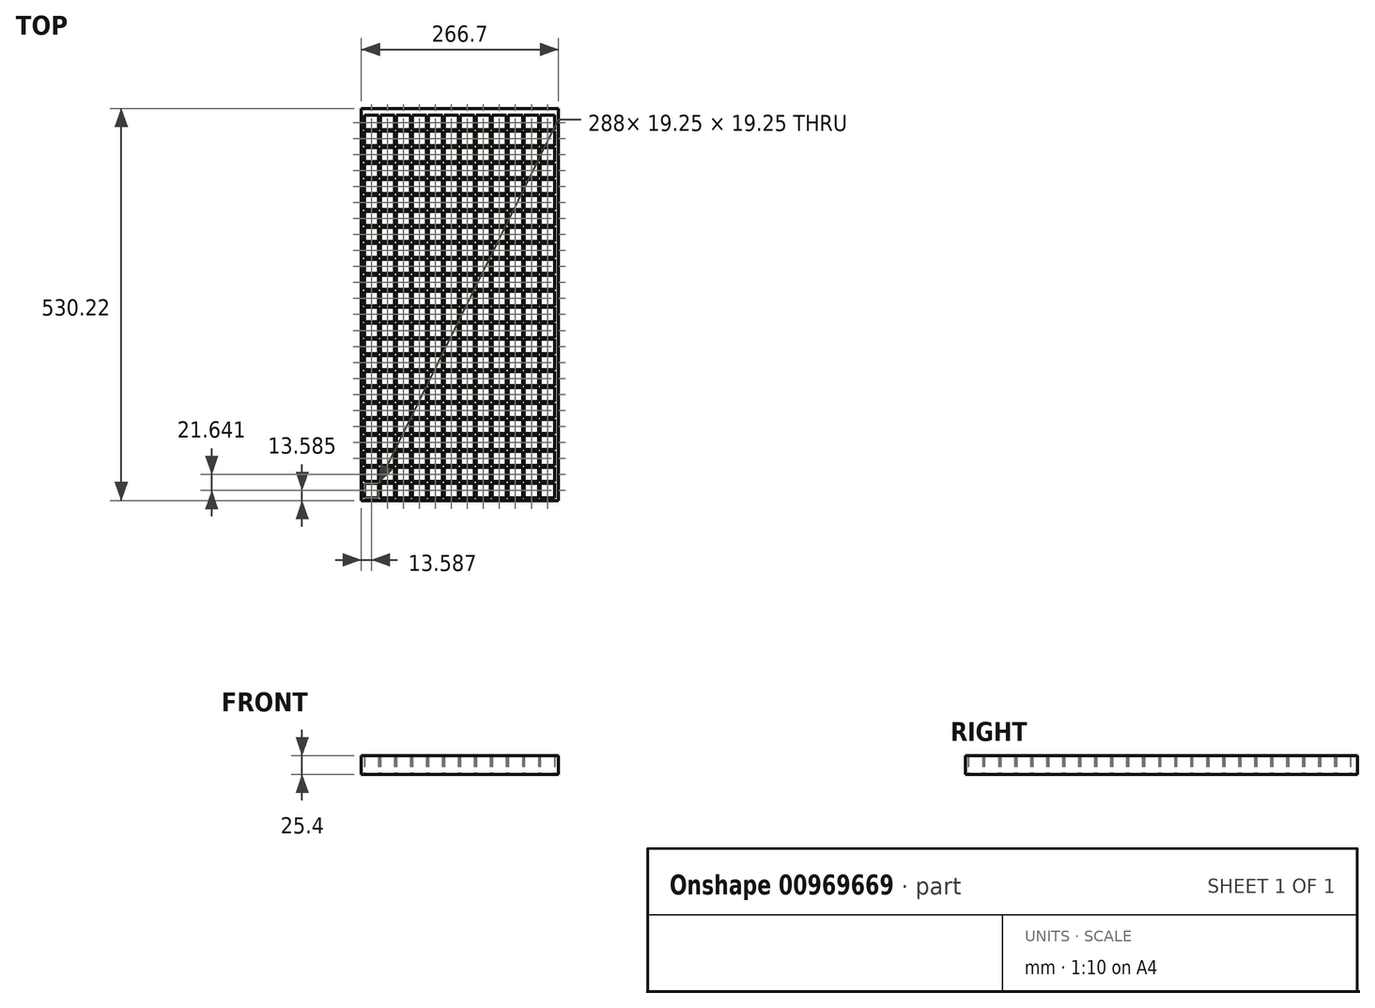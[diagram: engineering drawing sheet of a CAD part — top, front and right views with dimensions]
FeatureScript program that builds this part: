
annotation { "Feature Type Name" : "Feature", "Feature Type Description" : "" }
export const myFeature = defineFeature(function(context is Context, id is Id, definition is map)
    precondition{}
    {
        {
            var Q0;
            Q0=qCreatedBy(makeId("Top.planeOp"),FACE);
            var sketch = newSketch(context, id + "F0", { "sketchPlane" : qUnion([Q0])});
            skLineSegment(sketch, "E0.bottom", {"start": v(-120.4, -242.61) * mm, "end": v(146.3, -242.61) * mm});
            skLineSegment(sketch, "E0.top", {"start": v(-120.4, 287.61) * mm, "end": v(146.3, 287.61) * mm});
            skLineSegment(sketch, "E0.left", {"start": v(-120.4, -242.61) * mm, "end": v(-120.4, 287.61) * mm});
            skLineSegment(sketch, "E0.right", {"start": v(146.3, -242.61) * mm, "end": v(146.3, 287.61) * mm});
            skLineSegment(sketch, "E1.bottom", {"start": v(-116.43, -219.4) * mm, "end": v(-97.18, -219.4) * mm});
            skLineSegment(sketch, "E1.top", {"start": v(-116.43, -238.65) * mm, "end": v(-97.18, -238.65) * mm});
            skLineSegment(sketch, "E1.left", {"start": v(-116.43, -219.4) * mm, "end": v(-116.43, -238.65) * mm});
            skLineSegment(sketch, "E1.right", {"start": v(-97.18, -219.4) * mm, "end": v(-97.18, -238.65) * mm});
            skLineSegment(sketch, "E2.0.1.0", {"start": v(-116.43, -197.76) * mm, "end": v(-97.18, -197.76) * mm});
            skLineSegment(sketch, "E2.0.1.1", {"start": v(-116.43, -217.01) * mm, "end": v(-97.18, -217.01) * mm});
            skLineSegment(sketch, "E2.0.1.2", {"start": v(-116.43, -197.76) * mm, "end": v(-116.43, -217.01) * mm});
            skLineSegment(sketch, "E2.0.1.3", {"start": v(-97.18, -197.76) * mm, "end": v(-97.18, -217.01) * mm});
            skLineSegment(sketch, "E2.0.2.0", {"start": v(-116.43, -176.12) * mm, "end": v(-97.18, -176.12) * mm});
            skLineSegment(sketch, "E2.0.2.1", {"start": v(-116.43, -195.37) * mm, "end": v(-97.18, -195.37) * mm});
            skLineSegment(sketch, "E2.0.2.2", {"start": v(-116.43, -176.12) * mm, "end": v(-116.43, -195.37) * mm});
            skLineSegment(sketch, "E2.0.2.3", {"start": v(-97.18, -176.12) * mm, "end": v(-97.18, -195.37) * mm});
            skLineSegment(sketch, "E2.0.3.0", {"start": v(-116.43, -154.48) * mm, "end": v(-97.18, -154.48) * mm});
            skLineSegment(sketch, "E2.0.3.1", {"start": v(-116.43, -173.73) * mm, "end": v(-97.18, -173.73) * mm});
            skLineSegment(sketch, "E2.0.3.2", {"start": v(-116.43, -154.48) * mm, "end": v(-116.43, -173.73) * mm});
            skLineSegment(sketch, "E2.0.3.3", {"start": v(-97.18, -154.48) * mm, "end": v(-97.18, -173.73) * mm});
            skLineSegment(sketch, "E2.0.4.0", {"start": v(-116.43, -132.84) * mm, "end": v(-97.18, -132.84) * mm});
            skLineSegment(sketch, "E2.0.4.1", {"start": v(-116.43, -152.09) * mm, "end": v(-97.18, -152.09) * mm});
            skLineSegment(sketch, "E2.0.4.2", {"start": v(-116.43, -132.84) * mm, "end": v(-116.43, -152.09) * mm});
            skLineSegment(sketch, "E2.0.4.3", {"start": v(-97.18, -132.84) * mm, "end": v(-97.18, -152.09) * mm});
            skLineSegment(sketch, "E2.0.5.0", {"start": v(-116.43, -111.2) * mm, "end": v(-97.18, -111.2) * mm});
            skLineSegment(sketch, "E2.0.5.1", {"start": v(-116.43, -130.45) * mm, "end": v(-97.18, -130.45) * mm});
            skLineSegment(sketch, "E2.0.5.2", {"start": v(-116.43, -111.2) * mm, "end": v(-116.43, -130.45) * mm});
            skLineSegment(sketch, "E2.0.5.3", {"start": v(-97.18, -111.2) * mm, "end": v(-97.18, -130.45) * mm});
            skLineSegment(sketch, "E2.0.6.0", {"start": v(-116.43, -89.55) * mm, "end": v(-97.18, -89.55) * mm});
            skLineSegment(sketch, "E2.0.6.1", {"start": v(-116.43, -108.8) * mm, "end": v(-97.18, -108.8) * mm});
            skLineSegment(sketch, "E2.0.6.2", {"start": v(-116.43, -89.55) * mm, "end": v(-116.43, -108.8) * mm});
            skLineSegment(sketch, "E2.0.6.3", {"start": v(-97.18, -89.55) * mm, "end": v(-97.18, -108.8) * mm});
            skLineSegment(sketch, "E2.0.7.0", {"start": v(-116.43, -67.91) * mm, "end": v(-97.18, -67.91) * mm});
            skLineSegment(sketch, "E2.0.7.1", {"start": v(-116.43, -87.17) * mm, "end": v(-97.18, -87.17) * mm});
            skLineSegment(sketch, "E2.0.7.2", {"start": v(-116.43, -67.91) * mm, "end": v(-116.43, -87.17) * mm});
            skLineSegment(sketch, "E2.0.7.3", {"start": v(-97.18, -67.91) * mm, "end": v(-97.18, -87.17) * mm});
            skLineSegment(sketch, "E2.0.8.0", {"start": v(-116.43, -46.27) * mm, "end": v(-97.18, -46.27) * mm});
            skLineSegment(sketch, "E2.0.8.1", {"start": v(-116.43, -65.53) * mm, "end": v(-97.18, -65.53) * mm});
            skLineSegment(sketch, "E2.0.8.2", {"start": v(-116.43, -46.27) * mm, "end": v(-116.43, -65.53) * mm});
            skLineSegment(sketch, "E2.0.8.3", {"start": v(-97.18, -46.27) * mm, "end": v(-97.18, -65.53) * mm});
            skLineSegment(sketch, "E2.0.9.0", {"start": v(-116.43, -24.63) * mm, "end": v(-97.18, -24.63) * mm});
            skLineSegment(sketch, "E2.0.9.1", {"start": v(-116.43, -43.88) * mm, "end": v(-97.18, -43.88) * mm});
            skLineSegment(sketch, "E2.0.9.2", {"start": v(-116.43, -24.63) * mm, "end": v(-116.43, -43.88) * mm});
            skLineSegment(sketch, "E2.0.9.3", {"start": v(-97.18, -24.63) * mm, "end": v(-97.18, -43.88) * mm});
            skLineSegment(sketch, "E2.0.10.0", {"start": v(-116.43, -3) * mm, "end": v(-97.18, -3) * mm});
            skLineSegment(sketch, "E2.0.10.1", {"start": v(-116.43, -22.24) * mm, "end": v(-97.18, -22.24) * mm});
            skLineSegment(sketch, "E2.0.10.2", {"start": v(-116.43, -3) * mm, "end": v(-116.43, -22.24) * mm});
            skLineSegment(sketch, "E2.0.10.3", {"start": v(-97.18, -3) * mm, "end": v(-97.18, -22.24) * mm});
            skLineSegment(sketch, "E2.0.11.0", {"start": v(-116.43, 18.65) * mm, "end": v(-97.18, 18.65) * mm});
            skLineSegment(sketch, "E2.0.11.1", {"start": v(-116.43, -0.6) * mm, "end": v(-97.18, -0.6) * mm});
            skLineSegment(sketch, "E2.0.11.2", {"start": v(-116.43, 18.65) * mm, "end": v(-116.43, -0.6) * mm});
            skLineSegment(sketch, "E2.0.11.3", {"start": v(-97.18, 18.65) * mm, "end": v(-97.18, -0.6) * mm});
            skLineSegment(sketch, "E2.0.12.0", {"start": v(-116.43, 40.3) * mm, "end": v(-97.18, 40.3) * mm});
            skLineSegment(sketch, "E2.0.12.1", {"start": v(-116.43, 21.04) * mm, "end": v(-97.18, 21.04) * mm});
            skLineSegment(sketch, "E2.0.12.2", {"start": v(-116.43, 40.3) * mm, "end": v(-116.43, 21.04) * mm});
            skLineSegment(sketch, "E2.0.12.3", {"start": v(-97.18, 40.3) * mm, "end": v(-97.18, 21.04) * mm});
            skLineSegment(sketch, "E2.0.13.0", {"start": v(-116.43, 61.93) * mm, "end": v(-97.18, 61.93) * mm});
            skLineSegment(sketch, "E2.0.13.1", {"start": v(-116.43, 42.68) * mm, "end": v(-97.18, 42.68) * mm});
            skLineSegment(sketch, "E2.0.13.2", {"start": v(-116.43, 61.93) * mm, "end": v(-116.43, 42.68) * mm});
            skLineSegment(sketch, "E2.0.13.3", {"start": v(-97.18, 61.93) * mm, "end": v(-97.18, 42.68) * mm});
            skLineSegment(sketch, "E2.0.14.0", {"start": v(-116.43, 83.57) * mm, "end": v(-97.18, 83.57) * mm});
            skLineSegment(sketch, "E2.0.14.1", {"start": v(-116.43, 64.32) * mm, "end": v(-97.18, 64.32) * mm});
            skLineSegment(sketch, "E2.0.14.2", {"start": v(-116.43, 83.57) * mm, "end": v(-116.43, 64.32) * mm});
            skLineSegment(sketch, "E2.0.14.3", {"start": v(-97.18, 83.57) * mm, "end": v(-97.18, 64.32) * mm});
            skLineSegment(sketch, "E2.0.15.0", {"start": v(-116.43, 105.21) * mm, "end": v(-97.18, 105.21) * mm});
            skLineSegment(sketch, "E2.0.15.1", {"start": v(-116.43, 85.96) * mm, "end": v(-97.18, 85.96) * mm});
            skLineSegment(sketch, "E2.0.15.2", {"start": v(-116.43, 105.21) * mm, "end": v(-116.43, 85.96) * mm});
            skLineSegment(sketch, "E2.0.15.3", {"start": v(-97.18, 105.21) * mm, "end": v(-97.18, 85.96) * mm});
            skLineSegment(sketch, "E2.0.16.0", {"start": v(-116.43, 126.85) * mm, "end": v(-97.18, 126.85) * mm});
            skLineSegment(sketch, "E2.0.16.1", {"start": v(-116.43, 107.6) * mm, "end": v(-97.18, 107.6) * mm});
            skLineSegment(sketch, "E2.0.16.2", {"start": v(-116.43, 126.85) * mm, "end": v(-116.43, 107.6) * mm});
            skLineSegment(sketch, "E2.0.16.3", {"start": v(-97.18, 126.85) * mm, "end": v(-97.18, 107.6) * mm});
            skLineSegment(sketch, "E2.0.17.0", {"start": v(-116.43, 148.5) * mm, "end": v(-97.18, 148.5) * mm});
            skLineSegment(sketch, "E2.0.17.1", {"start": v(-116.43, 129.24) * mm, "end": v(-97.18, 129.24) * mm});
            skLineSegment(sketch, "E2.0.17.2", {"start": v(-116.43, 148.5) * mm, "end": v(-116.43, 129.24) * mm});
            skLineSegment(sketch, "E2.0.17.3", {"start": v(-97.18, 148.5) * mm, "end": v(-97.18, 129.24) * mm});
            skLineSegment(sketch, "E2.0.18.0", {"start": v(-116.43, 170.14) * mm, "end": v(-97.18, 170.14) * mm});
            skLineSegment(sketch, "E2.0.18.1", {"start": v(-116.43, 150.88) * mm, "end": v(-97.18, 150.88) * mm});
            skLineSegment(sketch, "E2.0.18.2", {"start": v(-116.43, 170.14) * mm, "end": v(-116.43, 150.88) * mm});
            skLineSegment(sketch, "E2.0.18.3", {"start": v(-97.18, 170.14) * mm, "end": v(-97.18, 150.88) * mm});
            skLineSegment(sketch, "E2.0.19.0", {"start": v(-116.43, 191.78) * mm, "end": v(-97.18, 191.78) * mm});
            skLineSegment(sketch, "E2.0.19.1", {"start": v(-116.43, 172.52) * mm, "end": v(-97.18, 172.52) * mm});
            skLineSegment(sketch, "E2.0.19.2", {"start": v(-116.43, 191.78) * mm, "end": v(-116.43, 172.52) * mm});
            skLineSegment(sketch, "E2.0.19.3", {"start": v(-97.18, 191.78) * mm, "end": v(-97.18, 172.52) * mm});
            skLineSegment(sketch, "E2.0.20.0", {"start": v(-116.43, 213.42) * mm, "end": v(-97.18, 213.42) * mm});
            skLineSegment(sketch, "E2.0.20.1", {"start": v(-116.43, 194.16) * mm, "end": v(-97.18, 194.16) * mm});
            skLineSegment(sketch, "E2.0.20.2", {"start": v(-116.43, 213.42) * mm, "end": v(-116.43, 194.16) * mm});
            skLineSegment(sketch, "E2.0.20.3", {"start": v(-97.18, 213.42) * mm, "end": v(-97.18, 194.16) * mm});
            skLineSegment(sketch, "E2.0.21.0", {"start": v(-116.43, 235.06) * mm, "end": v(-97.18, 235.06) * mm});
            skLineSegment(sketch, "E2.0.21.1", {"start": v(-116.43, 215.8) * mm, "end": v(-97.18, 215.8) * mm});
            skLineSegment(sketch, "E2.0.21.2", {"start": v(-116.43, 235.06) * mm, "end": v(-116.43, 215.8) * mm});
            skLineSegment(sketch, "E2.0.21.3", {"start": v(-97.18, 235.06) * mm, "end": v(-97.18, 215.8) * mm});
            skLineSegment(sketch, "E2.0.22.0", {"start": v(-116.43, 256.7) * mm, "end": v(-97.18, 256.7) * mm});
            skLineSegment(sketch, "E2.0.22.1", {"start": v(-116.43, 237.45) * mm, "end": v(-97.18, 237.45) * mm});
            skLineSegment(sketch, "E2.0.22.2", {"start": v(-116.43, 256.7) * mm, "end": v(-116.43, 237.45) * mm});
            skLineSegment(sketch, "E2.0.22.3", {"start": v(-97.18, 256.7) * mm, "end": v(-97.18, 237.45) * mm});
            skLineSegment(sketch, "E2.0.23.0", {"start": v(-116.43, 278.34) * mm, "end": v(-97.18, 278.34) * mm});
            skLineSegment(sketch, "E2.0.23.1", {"start": v(-116.43, 259.09) * mm, "end": v(-97.18, 259.09) * mm});
            skLineSegment(sketch, "E2.0.23.2", {"start": v(-116.43, 278.34) * mm, "end": v(-116.43, 259.09) * mm});
            skLineSegment(sketch, "E2.0.23.3", {"start": v(-97.18, 278.34) * mm, "end": v(-97.18, 259.09) * mm});
            skLineSegment(sketch, "E2.1.0.0", {"start": v(-94.79, -219.4) * mm, "end": v(-75.54, -219.4) * mm});
            skLineSegment(sketch, "E2.1.0.1", {"start": v(-94.79, -238.65) * mm, "end": v(-75.54, -238.65) * mm});
            skLineSegment(sketch, "E2.1.0.2", {"start": v(-94.79, -219.4) * mm, "end": v(-94.79, -238.65) * mm});
            skLineSegment(sketch, "E2.1.0.3", {"start": v(-75.54, -219.4) * mm, "end": v(-75.54, -238.65) * mm});
            skLineSegment(sketch, "E2.1.1.0", {"start": v(-94.79, -197.76) * mm, "end": v(-75.54, -197.76) * mm});
            skLineSegment(sketch, "E2.1.1.1", {"start": v(-94.79, -217.01) * mm, "end": v(-75.54, -217.01) * mm});
            skLineSegment(sketch, "E2.1.1.2", {"start": v(-94.79, -197.76) * mm, "end": v(-94.79, -217.01) * mm});
            skLineSegment(sketch, "E2.1.1.3", {"start": v(-75.54, -197.76) * mm, "end": v(-75.54, -217.01) * mm});
            skLineSegment(sketch, "E2.1.2.0", {"start": v(-94.79, -176.12) * mm, "end": v(-75.54, -176.12) * mm});
            skLineSegment(sketch, "E2.1.2.1", {"start": v(-94.79, -195.37) * mm, "end": v(-75.54, -195.37) * mm});
            skLineSegment(sketch, "E2.1.2.2", {"start": v(-94.79, -176.12) * mm, "end": v(-94.79, -195.37) * mm});
            skLineSegment(sketch, "E2.1.2.3", {"start": v(-75.54, -176.12) * mm, "end": v(-75.54, -195.37) * mm});
            skLineSegment(sketch, "E2.1.3.0", {"start": v(-94.79, -154.48) * mm, "end": v(-75.54, -154.48) * mm});
            skLineSegment(sketch, "E2.1.3.1", {"start": v(-94.79, -173.73) * mm, "end": v(-75.54, -173.73) * mm});
            skLineSegment(sketch, "E2.1.3.2", {"start": v(-94.79, -154.48) * mm, "end": v(-94.79, -173.73) * mm});
            skLineSegment(sketch, "E2.1.3.3", {"start": v(-75.54, -154.48) * mm, "end": v(-75.54, -173.73) * mm});
            skLineSegment(sketch, "E2.1.4.0", {"start": v(-94.79, -132.84) * mm, "end": v(-75.54, -132.84) * mm});
            skLineSegment(sketch, "E2.1.4.1", {"start": v(-94.79, -152.09) * mm, "end": v(-75.54, -152.09) * mm});
            skLineSegment(sketch, "E2.1.4.2", {"start": v(-94.79, -132.84) * mm, "end": v(-94.79, -152.09) * mm});
            skLineSegment(sketch, "E2.1.4.3", {"start": v(-75.54, -132.84) * mm, "end": v(-75.54, -152.09) * mm});
            skLineSegment(sketch, "E2.1.5.0", {"start": v(-94.79, -111.2) * mm, "end": v(-75.54, -111.2) * mm});
            skLineSegment(sketch, "E2.1.5.1", {"start": v(-94.79, -130.45) * mm, "end": v(-75.54, -130.45) * mm});
            skLineSegment(sketch, "E2.1.5.2", {"start": v(-94.79, -111.2) * mm, "end": v(-94.79, -130.45) * mm});
            skLineSegment(sketch, "E2.1.5.3", {"start": v(-75.54, -111.2) * mm, "end": v(-75.54, -130.45) * mm});
            skLineSegment(sketch, "E2.1.6.0", {"start": v(-94.79, -89.55) * mm, "end": v(-75.54, -89.55) * mm});
            skLineSegment(sketch, "E2.1.6.1", {"start": v(-94.79, -108.8) * mm, "end": v(-75.54, -108.8) * mm});
            skLineSegment(sketch, "E2.1.6.2", {"start": v(-94.79, -89.55) * mm, "end": v(-94.79, -108.8) * mm});
            skLineSegment(sketch, "E2.1.6.3", {"start": v(-75.54, -89.55) * mm, "end": v(-75.54, -108.8) * mm});
            skLineSegment(sketch, "E2.1.7.0", {"start": v(-94.79, -67.91) * mm, "end": v(-75.54, -67.91) * mm});
            skLineSegment(sketch, "E2.1.7.1", {"start": v(-94.79, -87.17) * mm, "end": v(-75.54, -87.17) * mm});
            skLineSegment(sketch, "E2.1.7.2", {"start": v(-94.79, -67.91) * mm, "end": v(-94.79, -87.17) * mm});
            skLineSegment(sketch, "E2.1.7.3", {"start": v(-75.54, -67.91) * mm, "end": v(-75.54, -87.17) * mm});
            skLineSegment(sketch, "E2.1.8.0", {"start": v(-94.79, -46.27) * mm, "end": v(-75.54, -46.27) * mm});
            skLineSegment(sketch, "E2.1.8.1", {"start": v(-94.79, -65.53) * mm, "end": v(-75.54, -65.53) * mm});
            skLineSegment(sketch, "E2.1.8.2", {"start": v(-94.79, -46.27) * mm, "end": v(-94.79, -65.53) * mm});
            skLineSegment(sketch, "E2.1.8.3", {"start": v(-75.54, -46.27) * mm, "end": v(-75.54, -65.53) * mm});
            skLineSegment(sketch, "E2.1.9.0", {"start": v(-94.79, -24.63) * mm, "end": v(-75.54, -24.63) * mm});
            skLineSegment(sketch, "E2.1.9.1", {"start": v(-94.79, -43.88) * mm, "end": v(-75.54, -43.88) * mm});
            skLineSegment(sketch, "E2.1.9.2", {"start": v(-94.79, -24.63) * mm, "end": v(-94.79, -43.88) * mm});
            skLineSegment(sketch, "E2.1.9.3", {"start": v(-75.54, -24.63) * mm, "end": v(-75.54, -43.88) * mm});
            skLineSegment(sketch, "E2.1.10.0", {"start": v(-94.79, -3) * mm, "end": v(-75.54, -3) * mm});
            skLineSegment(sketch, "E2.1.10.1", {"start": v(-94.79, -22.24) * mm, "end": v(-75.54, -22.24) * mm});
            skLineSegment(sketch, "E2.1.10.2", {"start": v(-94.79, -3) * mm, "end": v(-94.79, -22.24) * mm});
            skLineSegment(sketch, "E2.1.10.3", {"start": v(-75.54, -3) * mm, "end": v(-75.54, -22.24) * mm});
            skLineSegment(sketch, "E2.1.11.0", {"start": v(-94.79, 18.65) * mm, "end": v(-75.54, 18.65) * mm});
            skLineSegment(sketch, "E2.1.11.1", {"start": v(-94.79, -0.6) * mm, "end": v(-75.54, -0.6) * mm});
            skLineSegment(sketch, "E2.1.11.2", {"start": v(-94.79, 18.65) * mm, "end": v(-94.79, -0.6) * mm});
            skLineSegment(sketch, "E2.1.11.3", {"start": v(-75.54, 18.65) * mm, "end": v(-75.54, -0.6) * mm});
            skLineSegment(sketch, "E2.1.12.0", {"start": v(-94.79, 40.3) * mm, "end": v(-75.54, 40.3) * mm});
            skLineSegment(sketch, "E2.1.12.1", {"start": v(-94.79, 21.04) * mm, "end": v(-75.54, 21.04) * mm});
            skLineSegment(sketch, "E2.1.12.2", {"start": v(-94.79, 40.3) * mm, "end": v(-94.79, 21.04) * mm});
            skLineSegment(sketch, "E2.1.12.3", {"start": v(-75.54, 40.3) * mm, "end": v(-75.54, 21.04) * mm});
            skLineSegment(sketch, "E2.1.13.0", {"start": v(-94.79, 61.93) * mm, "end": v(-75.54, 61.93) * mm});
            skLineSegment(sketch, "E2.1.13.1", {"start": v(-94.79, 42.68) * mm, "end": v(-75.54, 42.68) * mm});
            skLineSegment(sketch, "E2.1.13.2", {"start": v(-94.79, 61.93) * mm, "end": v(-94.79, 42.68) * mm});
            skLineSegment(sketch, "E2.1.13.3", {"start": v(-75.54, 61.93) * mm, "end": v(-75.54, 42.68) * mm});
            skLineSegment(sketch, "E2.1.14.0", {"start": v(-94.79, 83.57) * mm, "end": v(-75.54, 83.57) * mm});
            skLineSegment(sketch, "E2.1.14.1", {"start": v(-94.79, 64.32) * mm, "end": v(-75.54, 64.32) * mm});
            skLineSegment(sketch, "E2.1.14.2", {"start": v(-94.79, 83.57) * mm, "end": v(-94.79, 64.32) * mm});
            skLineSegment(sketch, "E2.1.14.3", {"start": v(-75.54, 83.57) * mm, "end": v(-75.54, 64.32) * mm});
            skLineSegment(sketch, "E2.1.15.0", {"start": v(-94.79, 105.21) * mm, "end": v(-75.54, 105.21) * mm});
            skLineSegment(sketch, "E2.1.15.1", {"start": v(-94.79, 85.96) * mm, "end": v(-75.54, 85.96) * mm});
            skLineSegment(sketch, "E2.1.15.2", {"start": v(-94.79, 105.21) * mm, "end": v(-94.79, 85.96) * mm});
            skLineSegment(sketch, "E2.1.15.3", {"start": v(-75.54, 105.21) * mm, "end": v(-75.54, 85.96) * mm});
            skLineSegment(sketch, "E2.1.16.0", {"start": v(-94.79, 126.85) * mm, "end": v(-75.54, 126.85) * mm});
            skLineSegment(sketch, "E2.1.16.1", {"start": v(-94.79, 107.6) * mm, "end": v(-75.54, 107.6) * mm});
            skLineSegment(sketch, "E2.1.16.2", {"start": v(-94.79, 126.85) * mm, "end": v(-94.79, 107.6) * mm});
            skLineSegment(sketch, "E2.1.16.3", {"start": v(-75.54, 126.85) * mm, "end": v(-75.54, 107.6) * mm});
            skLineSegment(sketch, "E2.1.17.0", {"start": v(-94.79, 148.5) * mm, "end": v(-75.54, 148.5) * mm});
            skLineSegment(sketch, "E2.1.17.1", {"start": v(-94.79, 129.24) * mm, "end": v(-75.54, 129.24) * mm});
            skLineSegment(sketch, "E2.1.17.2", {"start": v(-94.79, 148.5) * mm, "end": v(-94.79, 129.24) * mm});
            skLineSegment(sketch, "E2.1.17.3", {"start": v(-75.54, 148.5) * mm, "end": v(-75.54, 129.24) * mm});
            skLineSegment(sketch, "E2.1.18.0", {"start": v(-94.79, 170.14) * mm, "end": v(-75.54, 170.14) * mm});
            skLineSegment(sketch, "E2.1.18.1", {"start": v(-94.79, 150.88) * mm, "end": v(-75.54, 150.88) * mm});
            skLineSegment(sketch, "E2.1.18.2", {"start": v(-94.79, 170.14) * mm, "end": v(-94.79, 150.88) * mm});
            skLineSegment(sketch, "E2.1.18.3", {"start": v(-75.54, 170.14) * mm, "end": v(-75.54, 150.88) * mm});
            skLineSegment(sketch, "E2.1.19.0", {"start": v(-94.79, 191.78) * mm, "end": v(-75.54, 191.78) * mm});
            skLineSegment(sketch, "E2.1.19.1", {"start": v(-94.79, 172.52) * mm, "end": v(-75.54, 172.52) * mm});
            skLineSegment(sketch, "E2.1.19.2", {"start": v(-94.79, 191.78) * mm, "end": v(-94.79, 172.52) * mm});
            skLineSegment(sketch, "E2.1.19.3", {"start": v(-75.54, 191.78) * mm, "end": v(-75.54, 172.52) * mm});
            skLineSegment(sketch, "E2.1.20.0", {"start": v(-94.79, 213.42) * mm, "end": v(-75.54, 213.42) * mm});
            skLineSegment(sketch, "E2.1.20.1", {"start": v(-94.79, 194.16) * mm, "end": v(-75.54, 194.16) * mm});
            skLineSegment(sketch, "E2.1.20.2", {"start": v(-94.79, 213.42) * mm, "end": v(-94.79, 194.16) * mm});
            skLineSegment(sketch, "E2.1.20.3", {"start": v(-75.54, 213.42) * mm, "end": v(-75.54, 194.16) * mm});
            skLineSegment(sketch, "E2.1.21.0", {"start": v(-94.79, 235.06) * mm, "end": v(-75.54, 235.06) * mm});
            skLineSegment(sketch, "E2.1.21.1", {"start": v(-94.79, 215.8) * mm, "end": v(-75.54, 215.8) * mm});
            skLineSegment(sketch, "E2.1.21.2", {"start": v(-94.79, 235.06) * mm, "end": v(-94.79, 215.8) * mm});
            skLineSegment(sketch, "E2.1.21.3", {"start": v(-75.54, 235.06) * mm, "end": v(-75.54, 215.8) * mm});
            skLineSegment(sketch, "E2.1.22.0", {"start": v(-94.79, 256.7) * mm, "end": v(-75.54, 256.7) * mm});
            skLineSegment(sketch, "E2.1.22.1", {"start": v(-94.79, 237.45) * mm, "end": v(-75.54, 237.45) * mm});
            skLineSegment(sketch, "E2.1.22.2", {"start": v(-94.79, 256.7) * mm, "end": v(-94.79, 237.45) * mm});
            skLineSegment(sketch, "E2.1.22.3", {"start": v(-75.54, 256.7) * mm, "end": v(-75.54, 237.45) * mm});
            skLineSegment(sketch, "E2.1.23.0", {"start": v(-94.79, 278.34) * mm, "end": v(-75.54, 278.34) * mm});
            skLineSegment(sketch, "E2.1.23.1", {"start": v(-94.79, 259.09) * mm, "end": v(-75.54, 259.09) * mm});
            skLineSegment(sketch, "E2.1.23.2", {"start": v(-94.79, 278.34) * mm, "end": v(-94.79, 259.09) * mm});
            skLineSegment(sketch, "E2.1.23.3", {"start": v(-75.54, 278.34) * mm, "end": v(-75.54, 259.09) * mm});
            skLineSegment(sketch, "E2.2.0.0", {"start": v(-73.15, -219.4) * mm, "end": v(-53.9, -219.4) * mm});
            skLineSegment(sketch, "E2.2.0.1", {"start": v(-73.15, -238.65) * mm, "end": v(-53.9, -238.65) * mm});
            skLineSegment(sketch, "E2.2.0.2", {"start": v(-73.15, -219.4) * mm, "end": v(-73.15, -238.65) * mm});
            skLineSegment(sketch, "E2.2.0.3", {"start": v(-53.9, -219.4) * mm, "end": v(-53.9, -238.65) * mm});
            skLineSegment(sketch, "E2.2.1.0", {"start": v(-73.15, -197.76) * mm, "end": v(-53.9, -197.76) * mm});
            skLineSegment(sketch, "E2.2.1.1", {"start": v(-73.15, -217.01) * mm, "end": v(-53.9, -217.01) * mm});
            skLineSegment(sketch, "E2.2.1.2", {"start": v(-73.15, -197.76) * mm, "end": v(-73.15, -217.01) * mm});
            skLineSegment(sketch, "E2.2.1.3", {"start": v(-53.9, -197.76) * mm, "end": v(-53.9, -217.01) * mm});
            skLineSegment(sketch, "E2.2.2.0", {"start": v(-73.15, -176.12) * mm, "end": v(-53.9, -176.12) * mm});
            skLineSegment(sketch, "E2.2.2.1", {"start": v(-73.15, -195.37) * mm, "end": v(-53.9, -195.37) * mm});
            skLineSegment(sketch, "E2.2.2.2", {"start": v(-73.15, -176.12) * mm, "end": v(-73.15, -195.37) * mm});
            skLineSegment(sketch, "E2.2.2.3", {"start": v(-53.9, -176.12) * mm, "end": v(-53.9, -195.37) * mm});
            skLineSegment(sketch, "E2.2.3.0", {"start": v(-73.15, -154.48) * mm, "end": v(-53.9, -154.48) * mm});
            skLineSegment(sketch, "E2.2.3.1", {"start": v(-73.15, -173.73) * mm, "end": v(-53.9, -173.73) * mm});
            skLineSegment(sketch, "E2.2.3.2", {"start": v(-73.15, -154.48) * mm, "end": v(-73.15, -173.73) * mm});
            skLineSegment(sketch, "E2.2.3.3", {"start": v(-53.9, -154.48) * mm, "end": v(-53.9, -173.73) * mm});
            skLineSegment(sketch, "E2.2.4.0", {"start": v(-73.15, -132.84) * mm, "end": v(-53.9, -132.84) * mm});
            skLineSegment(sketch, "E2.2.4.1", {"start": v(-73.15, -152.09) * mm, "end": v(-53.9, -152.09) * mm});
            skLineSegment(sketch, "E2.2.4.2", {"start": v(-73.15, -132.84) * mm, "end": v(-73.15, -152.09) * mm});
            skLineSegment(sketch, "E2.2.4.3", {"start": v(-53.9, -132.84) * mm, "end": v(-53.9, -152.09) * mm});
            skLineSegment(sketch, "E2.2.5.0", {"start": v(-73.15, -111.2) * mm, "end": v(-53.9, -111.2) * mm});
            skLineSegment(sketch, "E2.2.5.1", {"start": v(-73.15, -130.45) * mm, "end": v(-53.9, -130.45) * mm});
            skLineSegment(sketch, "E2.2.5.2", {"start": v(-73.15, -111.2) * mm, "end": v(-73.15, -130.45) * mm});
            skLineSegment(sketch, "E2.2.5.3", {"start": v(-53.9, -111.2) * mm, "end": v(-53.9, -130.45) * mm});
            skLineSegment(sketch, "E2.2.6.0", {"start": v(-73.15, -89.55) * mm, "end": v(-53.9, -89.55) * mm});
            skLineSegment(sketch, "E2.2.6.1", {"start": v(-73.15, -108.8) * mm, "end": v(-53.9, -108.8) * mm});
            skLineSegment(sketch, "E2.2.6.2", {"start": v(-73.15, -89.55) * mm, "end": v(-73.15, -108.8) * mm});
            skLineSegment(sketch, "E2.2.6.3", {"start": v(-53.9, -89.55) * mm, "end": v(-53.9, -108.8) * mm});
            skLineSegment(sketch, "E2.2.7.0", {"start": v(-73.15, -67.91) * mm, "end": v(-53.9, -67.91) * mm});
            skLineSegment(sketch, "E2.2.7.1", {"start": v(-73.15, -87.17) * mm, "end": v(-53.9, -87.17) * mm});
            skLineSegment(sketch, "E2.2.7.2", {"start": v(-73.15, -67.91) * mm, "end": v(-73.15, -87.17) * mm});
            skLineSegment(sketch, "E2.2.7.3", {"start": v(-53.9, -67.91) * mm, "end": v(-53.9, -87.17) * mm});
            skLineSegment(sketch, "E2.2.8.0", {"start": v(-73.15, -46.27) * mm, "end": v(-53.9, -46.27) * mm});
            skLineSegment(sketch, "E2.2.8.1", {"start": v(-73.15, -65.53) * mm, "end": v(-53.9, -65.53) * mm});
            skLineSegment(sketch, "E2.2.8.2", {"start": v(-73.15, -46.27) * mm, "end": v(-73.15, -65.53) * mm});
            skLineSegment(sketch, "E2.2.8.3", {"start": v(-53.9, -46.27) * mm, "end": v(-53.9, -65.53) * mm});
            skLineSegment(sketch, "E2.2.9.0", {"start": v(-73.15, -24.63) * mm, "end": v(-53.9, -24.63) * mm});
            skLineSegment(sketch, "E2.2.9.1", {"start": v(-73.15, -43.88) * mm, "end": v(-53.9, -43.88) * mm});
            skLineSegment(sketch, "E2.2.9.2", {"start": v(-73.15, -24.63) * mm, "end": v(-73.15, -43.88) * mm});
            skLineSegment(sketch, "E2.2.9.3", {"start": v(-53.9, -24.63) * mm, "end": v(-53.9, -43.88) * mm});
            skLineSegment(sketch, "E2.2.10.0", {"start": v(-73.15, -3) * mm, "end": v(-53.9, -3) * mm});
            skLineSegment(sketch, "E2.2.10.1", {"start": v(-73.15, -22.24) * mm, "end": v(-53.9, -22.24) * mm});
            skLineSegment(sketch, "E2.2.10.2", {"start": v(-73.15, -3) * mm, "end": v(-73.15, -22.24) * mm});
            skLineSegment(sketch, "E2.2.10.3", {"start": v(-53.9, -3) * mm, "end": v(-53.9, -22.24) * mm});
            skLineSegment(sketch, "E2.2.11.0", {"start": v(-73.15, 18.65) * mm, "end": v(-53.9, 18.65) * mm});
            skLineSegment(sketch, "E2.2.11.1", {"start": v(-73.15, -0.6) * mm, "end": v(-53.9, -0.6) * mm});
            skLineSegment(sketch, "E2.2.11.2", {"start": v(-73.15, 18.65) * mm, "end": v(-73.15, -0.6) * mm});
            skLineSegment(sketch, "E2.2.11.3", {"start": v(-53.9, 18.65) * mm, "end": v(-53.9, -0.6) * mm});
            skLineSegment(sketch, "E2.2.12.0", {"start": v(-73.15, 40.3) * mm, "end": v(-53.9, 40.3) * mm});
            skLineSegment(sketch, "E2.2.12.1", {"start": v(-73.15, 21.04) * mm, "end": v(-53.9, 21.04) * mm});
            skLineSegment(sketch, "E2.2.12.2", {"start": v(-73.15, 40.3) * mm, "end": v(-73.15, 21.04) * mm});
            skLineSegment(sketch, "E2.2.12.3", {"start": v(-53.9, 40.3) * mm, "end": v(-53.9, 21.04) * mm});
            skLineSegment(sketch, "E2.2.13.0", {"start": v(-73.15, 61.93) * mm, "end": v(-53.9, 61.93) * mm});
            skLineSegment(sketch, "E2.2.13.1", {"start": v(-73.15, 42.68) * mm, "end": v(-53.9, 42.68) * mm});
            skLineSegment(sketch, "E2.2.13.2", {"start": v(-73.15, 61.93) * mm, "end": v(-73.15, 42.68) * mm});
            skLineSegment(sketch, "E2.2.13.3", {"start": v(-53.9, 61.93) * mm, "end": v(-53.9, 42.68) * mm});
            skLineSegment(sketch, "E2.2.14.0", {"start": v(-73.15, 83.57) * mm, "end": v(-53.9, 83.57) * mm});
            skLineSegment(sketch, "E2.2.14.1", {"start": v(-73.15, 64.32) * mm, "end": v(-53.9, 64.32) * mm});
            skLineSegment(sketch, "E2.2.14.2", {"start": v(-73.15, 83.57) * mm, "end": v(-73.15, 64.32) * mm});
            skLineSegment(sketch, "E2.2.14.3", {"start": v(-53.9, 83.57) * mm, "end": v(-53.9, 64.32) * mm});
            skLineSegment(sketch, "E2.2.15.0", {"start": v(-73.15, 105.21) * mm, "end": v(-53.9, 105.21) * mm});
            skLineSegment(sketch, "E2.2.15.1", {"start": v(-73.15, 85.96) * mm, "end": v(-53.9, 85.96) * mm});
            skLineSegment(sketch, "E2.2.15.2", {"start": v(-73.15, 105.21) * mm, "end": v(-73.15, 85.96) * mm});
            skLineSegment(sketch, "E2.2.15.3", {"start": v(-53.9, 105.21) * mm, "end": v(-53.9, 85.96) * mm});
            skLineSegment(sketch, "E2.2.16.0", {"start": v(-73.15, 126.85) * mm, "end": v(-53.9, 126.85) * mm});
            skLineSegment(sketch, "E2.2.16.1", {"start": v(-73.15, 107.6) * mm, "end": v(-53.9, 107.6) * mm});
            skLineSegment(sketch, "E2.2.16.2", {"start": v(-73.15, 126.85) * mm, "end": v(-73.15, 107.6) * mm});
            skLineSegment(sketch, "E2.2.16.3", {"start": v(-53.9, 126.85) * mm, "end": v(-53.9, 107.6) * mm});
            skLineSegment(sketch, "E2.2.17.0", {"start": v(-73.15, 148.5) * mm, "end": v(-53.9, 148.5) * mm});
            skLineSegment(sketch, "E2.2.17.1", {"start": v(-73.15, 129.24) * mm, "end": v(-53.9, 129.24) * mm});
            skLineSegment(sketch, "E2.2.17.2", {"start": v(-73.15, 148.5) * mm, "end": v(-73.15, 129.24) * mm});
            skLineSegment(sketch, "E2.2.17.3", {"start": v(-53.9, 148.5) * mm, "end": v(-53.9, 129.24) * mm});
            skLineSegment(sketch, "E2.2.18.0", {"start": v(-73.15, 170.14) * mm, "end": v(-53.9, 170.14) * mm});
            skLineSegment(sketch, "E2.2.18.1", {"start": v(-73.15, 150.88) * mm, "end": v(-53.9, 150.88) * mm});
            skLineSegment(sketch, "E2.2.18.2", {"start": v(-73.15, 170.14) * mm, "end": v(-73.15, 150.88) * mm});
            skLineSegment(sketch, "E2.2.18.3", {"start": v(-53.9, 170.14) * mm, "end": v(-53.9, 150.88) * mm});
            skLineSegment(sketch, "E2.2.19.0", {"start": v(-73.15, 191.78) * mm, "end": v(-53.9, 191.78) * mm});
            skLineSegment(sketch, "E2.2.19.1", {"start": v(-73.15, 172.52) * mm, "end": v(-53.9, 172.52) * mm});
            skLineSegment(sketch, "E2.2.19.2", {"start": v(-73.15, 191.78) * mm, "end": v(-73.15, 172.52) * mm});
            skLineSegment(sketch, "E2.2.19.3", {"start": v(-53.9, 191.78) * mm, "end": v(-53.9, 172.52) * mm});
            skLineSegment(sketch, "E2.2.20.0", {"start": v(-73.15, 213.42) * mm, "end": v(-53.9, 213.42) * mm});
            skLineSegment(sketch, "E2.2.20.1", {"start": v(-73.15, 194.16) * mm, "end": v(-53.9, 194.16) * mm});
            skLineSegment(sketch, "E2.2.20.2", {"start": v(-73.15, 213.42) * mm, "end": v(-73.15, 194.16) * mm});
            skLineSegment(sketch, "E2.2.20.3", {"start": v(-53.9, 213.42) * mm, "end": v(-53.9, 194.16) * mm});
            skLineSegment(sketch, "E2.2.21.0", {"start": v(-73.15, 235.06) * mm, "end": v(-53.9, 235.06) * mm});
            skLineSegment(sketch, "E2.2.21.1", {"start": v(-73.15, 215.8) * mm, "end": v(-53.9, 215.8) * mm});
            skLineSegment(sketch, "E2.2.21.2", {"start": v(-73.15, 235.06) * mm, "end": v(-73.15, 215.8) * mm});
            skLineSegment(sketch, "E2.2.21.3", {"start": v(-53.9, 235.06) * mm, "end": v(-53.9, 215.8) * mm});
            skLineSegment(sketch, "E2.2.22.0", {"start": v(-73.15, 256.7) * mm, "end": v(-53.9, 256.7) * mm});
            skLineSegment(sketch, "E2.2.22.1", {"start": v(-73.15, 237.45) * mm, "end": v(-53.9, 237.45) * mm});
            skLineSegment(sketch, "E2.2.22.2", {"start": v(-73.15, 256.7) * mm, "end": v(-73.15, 237.45) * mm});
            skLineSegment(sketch, "E2.2.22.3", {"start": v(-53.9, 256.7) * mm, "end": v(-53.9, 237.45) * mm});
            skLineSegment(sketch, "E2.2.23.0", {"start": v(-73.15, 278.34) * mm, "end": v(-53.9, 278.34) * mm});
            skLineSegment(sketch, "E2.2.23.1", {"start": v(-73.15, 259.09) * mm, "end": v(-53.9, 259.09) * mm});
            skLineSegment(sketch, "E2.2.23.2", {"start": v(-73.15, 278.34) * mm, "end": v(-73.15, 259.09) * mm});
            skLineSegment(sketch, "E2.2.23.3", {"start": v(-53.9, 278.34) * mm, "end": v(-53.9, 259.09) * mm});
            skLineSegment(sketch, "E2.3.0.0", {"start": v(-51.5, -219.4) * mm, "end": v(-32.25, -219.4) * mm});
            skLineSegment(sketch, "E2.3.0.1", {"start": v(-51.5, -238.65) * mm, "end": v(-32.25, -238.65) * mm});
            skLineSegment(sketch, "E2.3.0.2", {"start": v(-51.5, -219.4) * mm, "end": v(-51.5, -238.65) * mm});
            skLineSegment(sketch, "E2.3.0.3", {"start": v(-32.25, -219.4) * mm, "end": v(-32.25, -238.65) * mm});
            skLineSegment(sketch, "E2.3.1.0", {"start": v(-51.5, -197.76) * mm, "end": v(-32.25, -197.76) * mm});
            skLineSegment(sketch, "E2.3.1.1", {"start": v(-51.5, -217.01) * mm, "end": v(-32.25, -217.01) * mm});
            skLineSegment(sketch, "E2.3.1.2", {"start": v(-51.5, -197.76) * mm, "end": v(-51.5, -217.01) * mm});
            skLineSegment(sketch, "E2.3.1.3", {"start": v(-32.25, -197.76) * mm, "end": v(-32.25, -217.01) * mm});
            skLineSegment(sketch, "E2.3.2.0", {"start": v(-51.5, -176.12) * mm, "end": v(-32.25, -176.12) * mm});
            skLineSegment(sketch, "E2.3.2.1", {"start": v(-51.5, -195.37) * mm, "end": v(-32.25, -195.37) * mm});
            skLineSegment(sketch, "E2.3.2.2", {"start": v(-51.5, -176.12) * mm, "end": v(-51.5, -195.37) * mm});
            skLineSegment(sketch, "E2.3.2.3", {"start": v(-32.25, -176.12) * mm, "end": v(-32.25, -195.37) * mm});
            skLineSegment(sketch, "E2.3.3.0", {"start": v(-51.5, -154.48) * mm, "end": v(-32.25, -154.48) * mm});
            skLineSegment(sketch, "E2.3.3.1", {"start": v(-51.5, -173.73) * mm, "end": v(-32.25, -173.73) * mm});
            skLineSegment(sketch, "E2.3.3.2", {"start": v(-51.5, -154.48) * mm, "end": v(-51.5, -173.73) * mm});
            skLineSegment(sketch, "E2.3.3.3", {"start": v(-32.25, -154.48) * mm, "end": v(-32.25, -173.73) * mm});
            skLineSegment(sketch, "E2.3.4.0", {"start": v(-51.5, -132.84) * mm, "end": v(-32.25, -132.84) * mm});
            skLineSegment(sketch, "E2.3.4.1", {"start": v(-51.5, -152.09) * mm, "end": v(-32.25, -152.09) * mm});
            skLineSegment(sketch, "E2.3.4.2", {"start": v(-51.5, -132.84) * mm, "end": v(-51.5, -152.09) * mm});
            skLineSegment(sketch, "E2.3.4.3", {"start": v(-32.25, -132.84) * mm, "end": v(-32.25, -152.09) * mm});
            skLineSegment(sketch, "E2.3.5.0", {"start": v(-51.5, -111.2) * mm, "end": v(-32.25, -111.2) * mm});
            skLineSegment(sketch, "E2.3.5.1", {"start": v(-51.5, -130.45) * mm, "end": v(-32.25, -130.45) * mm});
            skLineSegment(sketch, "E2.3.5.2", {"start": v(-51.5, -111.2) * mm, "end": v(-51.5, -130.45) * mm});
            skLineSegment(sketch, "E2.3.5.3", {"start": v(-32.25, -111.2) * mm, "end": v(-32.25, -130.45) * mm});
            skLineSegment(sketch, "E2.3.6.0", {"start": v(-51.5, -89.55) * mm, "end": v(-32.25, -89.55) * mm});
            skLineSegment(sketch, "E2.3.6.1", {"start": v(-51.5, -108.8) * mm, "end": v(-32.25, -108.8) * mm});
            skLineSegment(sketch, "E2.3.6.2", {"start": v(-51.5, -89.55) * mm, "end": v(-51.5, -108.8) * mm});
            skLineSegment(sketch, "E2.3.6.3", {"start": v(-32.25, -89.55) * mm, "end": v(-32.25, -108.8) * mm});
            skLineSegment(sketch, "E2.3.7.0", {"start": v(-51.5, -67.91) * mm, "end": v(-32.25, -67.91) * mm});
            skLineSegment(sketch, "E2.3.7.1", {"start": v(-51.5, -87.17) * mm, "end": v(-32.25, -87.17) * mm});
            skLineSegment(sketch, "E2.3.7.2", {"start": v(-51.5, -67.91) * mm, "end": v(-51.5, -87.17) * mm});
            skLineSegment(sketch, "E2.3.7.3", {"start": v(-32.25, -67.91) * mm, "end": v(-32.25, -87.17) * mm});
            skLineSegment(sketch, "E2.3.8.0", {"start": v(-51.5, -46.27) * mm, "end": v(-32.25, -46.27) * mm});
            skLineSegment(sketch, "E2.3.8.1", {"start": v(-51.5, -65.53) * mm, "end": v(-32.25, -65.53) * mm});
            skLineSegment(sketch, "E2.3.8.2", {"start": v(-51.5, -46.27) * mm, "end": v(-51.5, -65.53) * mm});
            skLineSegment(sketch, "E2.3.8.3", {"start": v(-32.25, -46.27) * mm, "end": v(-32.25, -65.53) * mm});
            skLineSegment(sketch, "E2.3.9.0", {"start": v(-51.5, -24.63) * mm, "end": v(-32.25, -24.63) * mm});
            skLineSegment(sketch, "E2.3.9.1", {"start": v(-51.5, -43.88) * mm, "end": v(-32.25, -43.88) * mm});
            skLineSegment(sketch, "E2.3.9.2", {"start": v(-51.5, -24.63) * mm, "end": v(-51.5, -43.88) * mm});
            skLineSegment(sketch, "E2.3.9.3", {"start": v(-32.25, -24.63) * mm, "end": v(-32.25, -43.88) * mm});
            skLineSegment(sketch, "E2.3.10.0", {"start": v(-51.5, -3) * mm, "end": v(-32.25, -3) * mm});
            skLineSegment(sketch, "E2.3.10.1", {"start": v(-51.5, -22.24) * mm, "end": v(-32.25, -22.24) * mm});
            skLineSegment(sketch, "E2.3.10.2", {"start": v(-51.5, -3) * mm, "end": v(-51.5, -22.24) * mm});
            skLineSegment(sketch, "E2.3.10.3", {"start": v(-32.25, -3) * mm, "end": v(-32.25, -22.24) * mm});
            skLineSegment(sketch, "E2.3.11.0", {"start": v(-51.5, 18.65) * mm, "end": v(-32.25, 18.65) * mm});
            skLineSegment(sketch, "E2.3.11.1", {"start": v(-51.5, -0.6) * mm, "end": v(-32.25, -0.6) * mm});
            skLineSegment(sketch, "E2.3.11.2", {"start": v(-51.5, 18.65) * mm, "end": v(-51.5, -0.6) * mm});
            skLineSegment(sketch, "E2.3.11.3", {"start": v(-32.25, 18.65) * mm, "end": v(-32.25, -0.6) * mm});
            skLineSegment(sketch, "E2.3.12.0", {"start": v(-51.5, 40.3) * mm, "end": v(-32.25, 40.3) * mm});
            skLineSegment(sketch, "E2.3.12.1", {"start": v(-51.5, 21.04) * mm, "end": v(-32.25, 21.04) * mm});
            skLineSegment(sketch, "E2.3.12.2", {"start": v(-51.5, 40.3) * mm, "end": v(-51.5, 21.04) * mm});
            skLineSegment(sketch, "E2.3.12.3", {"start": v(-32.25, 40.3) * mm, "end": v(-32.25, 21.04) * mm});
            skLineSegment(sketch, "E2.3.13.0", {"start": v(-51.5, 61.93) * mm, "end": v(-32.25, 61.93) * mm});
            skLineSegment(sketch, "E2.3.13.1", {"start": v(-51.5, 42.68) * mm, "end": v(-32.25, 42.68) * mm});
            skLineSegment(sketch, "E2.3.13.2", {"start": v(-51.5, 61.93) * mm, "end": v(-51.5, 42.68) * mm});
            skLineSegment(sketch, "E2.3.13.3", {"start": v(-32.25, 61.93) * mm, "end": v(-32.25, 42.68) * mm});
            skLineSegment(sketch, "E2.3.14.0", {"start": v(-51.5, 83.57) * mm, "end": v(-32.25, 83.57) * mm});
            skLineSegment(sketch, "E2.3.14.1", {"start": v(-51.5, 64.32) * mm, "end": v(-32.25, 64.32) * mm});
            skLineSegment(sketch, "E2.3.14.2", {"start": v(-51.5, 83.57) * mm, "end": v(-51.5, 64.32) * mm});
            skLineSegment(sketch, "E2.3.14.3", {"start": v(-32.25, 83.57) * mm, "end": v(-32.25, 64.32) * mm});
            skLineSegment(sketch, "E2.3.15.0", {"start": v(-51.5, 105.21) * mm, "end": v(-32.25, 105.21) * mm});
            skLineSegment(sketch, "E2.3.15.1", {"start": v(-51.5, 85.96) * mm, "end": v(-32.25, 85.96) * mm});
            skLineSegment(sketch, "E2.3.15.2", {"start": v(-51.5, 105.21) * mm, "end": v(-51.5, 85.96) * mm});
            skLineSegment(sketch, "E2.3.15.3", {"start": v(-32.25, 105.21) * mm, "end": v(-32.25, 85.96) * mm});
            skLineSegment(sketch, "E2.3.16.0", {"start": v(-51.5, 126.85) * mm, "end": v(-32.25, 126.85) * mm});
            skLineSegment(sketch, "E2.3.16.1", {"start": v(-51.5, 107.6) * mm, "end": v(-32.25, 107.6) * mm});
            skLineSegment(sketch, "E2.3.16.2", {"start": v(-51.5, 126.85) * mm, "end": v(-51.5, 107.6) * mm});
            skLineSegment(sketch, "E2.3.16.3", {"start": v(-32.25, 126.85) * mm, "end": v(-32.25, 107.6) * mm});
            skLineSegment(sketch, "E2.3.17.0", {"start": v(-51.5, 148.5) * mm, "end": v(-32.25, 148.5) * mm});
            skLineSegment(sketch, "E2.3.17.1", {"start": v(-51.5, 129.24) * mm, "end": v(-32.25, 129.24) * mm});
            skLineSegment(sketch, "E2.3.17.2", {"start": v(-51.5, 148.5) * mm, "end": v(-51.5, 129.24) * mm});
            skLineSegment(sketch, "E2.3.17.3", {"start": v(-32.25, 148.5) * mm, "end": v(-32.25, 129.24) * mm});
            skLineSegment(sketch, "E2.3.18.0", {"start": v(-51.5, 170.14) * mm, "end": v(-32.25, 170.14) * mm});
            skLineSegment(sketch, "E2.3.18.1", {"start": v(-51.5, 150.88) * mm, "end": v(-32.25, 150.88) * mm});
            skLineSegment(sketch, "E2.3.18.2", {"start": v(-51.5, 170.14) * mm, "end": v(-51.5, 150.88) * mm});
            skLineSegment(sketch, "E2.3.18.3", {"start": v(-32.25, 170.14) * mm, "end": v(-32.25, 150.88) * mm});
            skLineSegment(sketch, "E2.3.19.0", {"start": v(-51.5, 191.78) * mm, "end": v(-32.25, 191.78) * mm});
            skLineSegment(sketch, "E2.3.19.1", {"start": v(-51.5, 172.52) * mm, "end": v(-32.25, 172.52) * mm});
            skLineSegment(sketch, "E2.3.19.2", {"start": v(-51.5, 191.78) * mm, "end": v(-51.5, 172.52) * mm});
            skLineSegment(sketch, "E2.3.19.3", {"start": v(-32.25, 191.78) * mm, "end": v(-32.25, 172.52) * mm});
            skLineSegment(sketch, "E2.3.20.0", {"start": v(-51.5, 213.42) * mm, "end": v(-32.25, 213.42) * mm});
            skLineSegment(sketch, "E2.3.20.1", {"start": v(-51.5, 194.16) * mm, "end": v(-32.25, 194.16) * mm});
            skLineSegment(sketch, "E2.3.20.2", {"start": v(-51.5, 213.42) * mm, "end": v(-51.5, 194.16) * mm});
            skLineSegment(sketch, "E2.3.20.3", {"start": v(-32.25, 213.42) * mm, "end": v(-32.25, 194.16) * mm});
            skLineSegment(sketch, "E2.3.21.0", {"start": v(-51.5, 235.06) * mm, "end": v(-32.25, 235.06) * mm});
            skLineSegment(sketch, "E2.3.21.1", {"start": v(-51.5, 215.8) * mm, "end": v(-32.25, 215.8) * mm});
            skLineSegment(sketch, "E2.3.21.2", {"start": v(-51.5, 235.06) * mm, "end": v(-51.5, 215.8) * mm});
            skLineSegment(sketch, "E2.3.21.3", {"start": v(-32.25, 235.06) * mm, "end": v(-32.25, 215.8) * mm});
            skLineSegment(sketch, "E2.3.22.0", {"start": v(-51.5, 256.7) * mm, "end": v(-32.25, 256.7) * mm});
            skLineSegment(sketch, "E2.3.22.1", {"start": v(-51.5, 237.45) * mm, "end": v(-32.25, 237.45) * mm});
            skLineSegment(sketch, "E2.3.22.2", {"start": v(-51.5, 256.7) * mm, "end": v(-51.5, 237.45) * mm});
            skLineSegment(sketch, "E2.3.22.3", {"start": v(-32.25, 256.7) * mm, "end": v(-32.25, 237.45) * mm});
            skLineSegment(sketch, "E2.3.23.0", {"start": v(-51.5, 278.34) * mm, "end": v(-32.25, 278.34) * mm});
            skLineSegment(sketch, "E2.3.23.1", {"start": v(-51.5, 259.09) * mm, "end": v(-32.25, 259.09) * mm});
            skLineSegment(sketch, "E2.3.23.2", {"start": v(-51.5, 278.34) * mm, "end": v(-51.5, 259.09) * mm});
            skLineSegment(sketch, "E2.3.23.3", {"start": v(-32.25, 278.34) * mm, "end": v(-32.25, 259.09) * mm});
            skLineSegment(sketch, "E2.4.0.0", {"start": v(-29.87, -219.4) * mm, "end": v(-10.61, -219.4) * mm});
            skLineSegment(sketch, "E2.4.0.1", {"start": v(-29.87, -238.65) * mm, "end": v(-10.61, -238.65) * mm});
            skLineSegment(sketch, "E2.4.0.2", {"start": v(-29.87, -219.4) * mm, "end": v(-29.87, -238.65) * mm});
            skLineSegment(sketch, "E2.4.0.3", {"start": v(-10.61, -219.4) * mm, "end": v(-10.61, -238.65) * mm});
            skLineSegment(sketch, "E2.4.1.0", {"start": v(-29.87, -197.76) * mm, "end": v(-10.61, -197.76) * mm});
            skLineSegment(sketch, "E2.4.1.1", {"start": v(-29.87, -217.01) * mm, "end": v(-10.61, -217.01) * mm});
            skLineSegment(sketch, "E2.4.1.2", {"start": v(-29.87, -197.76) * mm, "end": v(-29.87, -217.01) * mm});
            skLineSegment(sketch, "E2.4.1.3", {"start": v(-10.61, -197.76) * mm, "end": v(-10.61, -217.01) * mm});
            skLineSegment(sketch, "E2.4.2.0", {"start": v(-29.87, -176.12) * mm, "end": v(-10.61, -176.12) * mm});
            skLineSegment(sketch, "E2.4.2.1", {"start": v(-29.87, -195.37) * mm, "end": v(-10.61, -195.37) * mm});
            skLineSegment(sketch, "E2.4.2.2", {"start": v(-29.87, -176.12) * mm, "end": v(-29.87, -195.37) * mm});
            skLineSegment(sketch, "E2.4.2.3", {"start": v(-10.61, -176.12) * mm, "end": v(-10.61, -195.37) * mm});
            skLineSegment(sketch, "E2.4.3.0", {"start": v(-29.87, -154.48) * mm, "end": v(-10.61, -154.48) * mm});
            skLineSegment(sketch, "E2.4.3.1", {"start": v(-29.87, -173.73) * mm, "end": v(-10.61, -173.73) * mm});
            skLineSegment(sketch, "E2.4.3.2", {"start": v(-29.87, -154.48) * mm, "end": v(-29.87, -173.73) * mm});
            skLineSegment(sketch, "E2.4.3.3", {"start": v(-10.61, -154.48) * mm, "end": v(-10.61, -173.73) * mm});
            skLineSegment(sketch, "E2.4.4.0", {"start": v(-29.87, -132.84) * mm, "end": v(-10.61, -132.84) * mm});
            skLineSegment(sketch, "E2.4.4.1", {"start": v(-29.87, -152.09) * mm, "end": v(-10.61, -152.09) * mm});
            skLineSegment(sketch, "E2.4.4.2", {"start": v(-29.87, -132.84) * mm, "end": v(-29.87, -152.09) * mm});
            skLineSegment(sketch, "E2.4.4.3", {"start": v(-10.61, -132.84) * mm, "end": v(-10.61, -152.09) * mm});
            skLineSegment(sketch, "E2.4.5.0", {"start": v(-29.87, -111.2) * mm, "end": v(-10.61, -111.2) * mm});
            skLineSegment(sketch, "E2.4.5.1", {"start": v(-29.87, -130.45) * mm, "end": v(-10.61, -130.45) * mm});
            skLineSegment(sketch, "E2.4.5.2", {"start": v(-29.87, -111.2) * mm, "end": v(-29.87, -130.45) * mm});
            skLineSegment(sketch, "E2.4.5.3", {"start": v(-10.61, -111.2) * mm, "end": v(-10.61, -130.45) * mm});
            skLineSegment(sketch, "E2.4.6.0", {"start": v(-29.87, -89.55) * mm, "end": v(-10.61, -89.55) * mm});
            skLineSegment(sketch, "E2.4.6.1", {"start": v(-29.87, -108.8) * mm, "end": v(-10.61, -108.8) * mm});
            skLineSegment(sketch, "E2.4.6.2", {"start": v(-29.87, -89.55) * mm, "end": v(-29.87, -108.8) * mm});
            skLineSegment(sketch, "E2.4.6.3", {"start": v(-10.61, -89.55) * mm, "end": v(-10.61, -108.8) * mm});
            skLineSegment(sketch, "E2.4.7.0", {"start": v(-29.87, -67.91) * mm, "end": v(-10.61, -67.91) * mm});
            skLineSegment(sketch, "E2.4.7.1", {"start": v(-29.87, -87.17) * mm, "end": v(-10.61, -87.17) * mm});
            skLineSegment(sketch, "E2.4.7.2", {"start": v(-29.87, -67.91) * mm, "end": v(-29.87, -87.17) * mm});
            skLineSegment(sketch, "E2.4.7.3", {"start": v(-10.61, -67.91) * mm, "end": v(-10.61, -87.17) * mm});
            skLineSegment(sketch, "E2.4.8.0", {"start": v(-29.87, -46.27) * mm, "end": v(-10.61, -46.27) * mm});
            skLineSegment(sketch, "E2.4.8.1", {"start": v(-29.87, -65.53) * mm, "end": v(-10.61, -65.53) * mm});
            skLineSegment(sketch, "E2.4.8.2", {"start": v(-29.87, -46.27) * mm, "end": v(-29.87, -65.53) * mm});
            skLineSegment(sketch, "E2.4.8.3", {"start": v(-10.61, -46.27) * mm, "end": v(-10.61, -65.53) * mm});
            skLineSegment(sketch, "E2.4.9.0", {"start": v(-29.87, -24.63) * mm, "end": v(-10.61, -24.63) * mm});
            skLineSegment(sketch, "E2.4.9.1", {"start": v(-29.87, -43.88) * mm, "end": v(-10.61, -43.88) * mm});
            skLineSegment(sketch, "E2.4.9.2", {"start": v(-29.87, -24.63) * mm, "end": v(-29.87, -43.88) * mm});
            skLineSegment(sketch, "E2.4.9.3", {"start": v(-10.61, -24.63) * mm, "end": v(-10.61, -43.88) * mm});
            skLineSegment(sketch, "E2.4.10.0", {"start": v(-29.87, -3) * mm, "end": v(-10.61, -3) * mm});
            skLineSegment(sketch, "E2.4.10.1", {"start": v(-29.87, -22.24) * mm, "end": v(-10.61, -22.24) * mm});
            skLineSegment(sketch, "E2.4.10.2", {"start": v(-29.87, -3) * mm, "end": v(-29.87, -22.24) * mm});
            skLineSegment(sketch, "E2.4.10.3", {"start": v(-10.61, -3) * mm, "end": v(-10.61, -22.24) * mm});
            skLineSegment(sketch, "E2.4.11.0", {"start": v(-29.87, 18.65) * mm, "end": v(-10.61, 18.65) * mm});
            skLineSegment(sketch, "E2.4.11.1", {"start": v(-29.87, -0.6) * mm, "end": v(-10.61, -0.6) * mm});
            skLineSegment(sketch, "E2.4.11.2", {"start": v(-29.87, 18.65) * mm, "end": v(-29.87, -0.6) * mm});
            skLineSegment(sketch, "E2.4.11.3", {"start": v(-10.61, 18.65) * mm, "end": v(-10.61, -0.6) * mm});
            skLineSegment(sketch, "E2.4.12.0", {"start": v(-29.87, 40.3) * mm, "end": v(-10.61, 40.3) * mm});
            skLineSegment(sketch, "E2.4.12.1", {"start": v(-29.87, 21.04) * mm, "end": v(-10.61, 21.04) * mm});
            skLineSegment(sketch, "E2.4.12.2", {"start": v(-29.87, 40.3) * mm, "end": v(-29.87, 21.04) * mm});
            skLineSegment(sketch, "E2.4.12.3", {"start": v(-10.61, 40.3) * mm, "end": v(-10.61, 21.04) * mm});
            skLineSegment(sketch, "E2.4.13.0", {"start": v(-29.87, 61.93) * mm, "end": v(-10.61, 61.93) * mm});
            skLineSegment(sketch, "E2.4.13.1", {"start": v(-29.87, 42.68) * mm, "end": v(-10.61, 42.68) * mm});
            skLineSegment(sketch, "E2.4.13.2", {"start": v(-29.87, 61.93) * mm, "end": v(-29.87, 42.68) * mm});
            skLineSegment(sketch, "E2.4.13.3", {"start": v(-10.61, 61.93) * mm, "end": v(-10.61, 42.68) * mm});
            skLineSegment(sketch, "E2.4.14.0", {"start": v(-29.87, 83.57) * mm, "end": v(-10.61, 83.57) * mm});
            skLineSegment(sketch, "E2.4.14.1", {"start": v(-29.87, 64.32) * mm, "end": v(-10.61, 64.32) * mm});
            skLineSegment(sketch, "E2.4.14.2", {"start": v(-29.87, 83.57) * mm, "end": v(-29.87, 64.32) * mm});
            skLineSegment(sketch, "E2.4.14.3", {"start": v(-10.61, 83.57) * mm, "end": v(-10.61, 64.32) * mm});
            skLineSegment(sketch, "E2.4.15.0", {"start": v(-29.87, 105.21) * mm, "end": v(-10.61, 105.21) * mm});
            skLineSegment(sketch, "E2.4.15.1", {"start": v(-29.87, 85.96) * mm, "end": v(-10.61, 85.96) * mm});
            skLineSegment(sketch, "E2.4.15.2", {"start": v(-29.87, 105.21) * mm, "end": v(-29.87, 85.96) * mm});
            skLineSegment(sketch, "E2.4.15.3", {"start": v(-10.61, 105.21) * mm, "end": v(-10.61, 85.96) * mm});
            skLineSegment(sketch, "E2.4.16.0", {"start": v(-29.87, 126.85) * mm, "end": v(-10.61, 126.85) * mm});
            skLineSegment(sketch, "E2.4.16.1", {"start": v(-29.87, 107.6) * mm, "end": v(-10.61, 107.6) * mm});
            skLineSegment(sketch, "E2.4.16.2", {"start": v(-29.87, 126.85) * mm, "end": v(-29.87, 107.6) * mm});
            skLineSegment(sketch, "E2.4.16.3", {"start": v(-10.61, 126.85) * mm, "end": v(-10.61, 107.6) * mm});
            skLineSegment(sketch, "E2.4.17.0", {"start": v(-29.87, 148.5) * mm, "end": v(-10.61, 148.5) * mm});
            skLineSegment(sketch, "E2.4.17.1", {"start": v(-29.87, 129.24) * mm, "end": v(-10.61, 129.24) * mm});
            skLineSegment(sketch, "E2.4.17.2", {"start": v(-29.87, 148.5) * mm, "end": v(-29.87, 129.24) * mm});
            skLineSegment(sketch, "E2.4.17.3", {"start": v(-10.61, 148.5) * mm, "end": v(-10.61, 129.24) * mm});
            skLineSegment(sketch, "E2.4.18.0", {"start": v(-29.87, 170.14) * mm, "end": v(-10.61, 170.14) * mm});
            skLineSegment(sketch, "E2.4.18.1", {"start": v(-29.87, 150.88) * mm, "end": v(-10.61, 150.88) * mm});
            skLineSegment(sketch, "E2.4.18.2", {"start": v(-29.87, 170.14) * mm, "end": v(-29.87, 150.88) * mm});
            skLineSegment(sketch, "E2.4.18.3", {"start": v(-10.61, 170.14) * mm, "end": v(-10.61, 150.88) * mm});
            skLineSegment(sketch, "E2.4.19.0", {"start": v(-29.87, 191.78) * mm, "end": v(-10.61, 191.78) * mm});
            skLineSegment(sketch, "E2.4.19.1", {"start": v(-29.87, 172.52) * mm, "end": v(-10.61, 172.52) * mm});
            skLineSegment(sketch, "E2.4.19.2", {"start": v(-29.87, 191.78) * mm, "end": v(-29.87, 172.52) * mm});
            skLineSegment(sketch, "E2.4.19.3", {"start": v(-10.61, 191.78) * mm, "end": v(-10.61, 172.52) * mm});
            skLineSegment(sketch, "E2.4.20.0", {"start": v(-29.87, 213.42) * mm, "end": v(-10.61, 213.42) * mm});
            skLineSegment(sketch, "E2.4.20.1", {"start": v(-29.87, 194.16) * mm, "end": v(-10.61, 194.16) * mm});
            skLineSegment(sketch, "E2.4.20.2", {"start": v(-29.87, 213.42) * mm, "end": v(-29.87, 194.16) * mm});
            skLineSegment(sketch, "E2.4.20.3", {"start": v(-10.61, 213.42) * mm, "end": v(-10.61, 194.16) * mm});
            skLineSegment(sketch, "E2.4.21.0", {"start": v(-29.87, 235.06) * mm, "end": v(-10.61, 235.06) * mm});
            skLineSegment(sketch, "E2.4.21.1", {"start": v(-29.87, 215.8) * mm, "end": v(-10.61, 215.8) * mm});
            skLineSegment(sketch, "E2.4.21.2", {"start": v(-29.87, 235.06) * mm, "end": v(-29.87, 215.8) * mm});
            skLineSegment(sketch, "E2.4.21.3", {"start": v(-10.61, 235.06) * mm, "end": v(-10.61, 215.8) * mm});
            skLineSegment(sketch, "E2.4.22.0", {"start": v(-29.87, 256.7) * mm, "end": v(-10.61, 256.7) * mm});
            skLineSegment(sketch, "E2.4.22.1", {"start": v(-29.87, 237.45) * mm, "end": v(-10.61, 237.45) * mm});
            skLineSegment(sketch, "E2.4.22.2", {"start": v(-29.87, 256.7) * mm, "end": v(-29.87, 237.45) * mm});
            skLineSegment(sketch, "E2.4.22.3", {"start": v(-10.61, 256.7) * mm, "end": v(-10.61, 237.45) * mm});
            skLineSegment(sketch, "E2.4.23.0", {"start": v(-29.87, 278.34) * mm, "end": v(-10.61, 278.34) * mm});
            skLineSegment(sketch, "E2.4.23.1", {"start": v(-29.87, 259.09) * mm, "end": v(-10.61, 259.09) * mm});
            skLineSegment(sketch, "E2.4.23.2", {"start": v(-29.87, 278.34) * mm, "end": v(-29.87, 259.09) * mm});
            skLineSegment(sketch, "E2.4.23.3", {"start": v(-10.61, 278.34) * mm, "end": v(-10.61, 259.09) * mm});
            skLineSegment(sketch, "E2.5.0.0", {"start": v(-8.23, -219.4) * mm, "end": v(11.03, -219.4) * mm});
            skLineSegment(sketch, "E2.5.0.1", {"start": v(-8.23, -238.65) * mm, "end": v(11.03, -238.65) * mm});
            skLineSegment(sketch, "E2.5.0.2", {"start": v(-8.23, -219.4) * mm, "end": v(-8.23, -238.65) * mm});
            skLineSegment(sketch, "E2.5.0.3", {"start": v(11.03, -219.4) * mm, "end": v(11.03, -238.65) * mm});
            skLineSegment(sketch, "E2.5.1.0", {"start": v(-8.23, -197.76) * mm, "end": v(11.03, -197.76) * mm});
            skLineSegment(sketch, "E2.5.1.1", {"start": v(-8.23, -217.01) * mm, "end": v(11.03, -217.01) * mm});
            skLineSegment(sketch, "E2.5.1.2", {"start": v(-8.23, -197.76) * mm, "end": v(-8.23, -217.01) * mm});
            skLineSegment(sketch, "E2.5.1.3", {"start": v(11.03, -197.76) * mm, "end": v(11.03, -217.01) * mm});
            skLineSegment(sketch, "E2.5.2.0", {"start": v(-8.23, -176.12) * mm, "end": v(11.03, -176.12) * mm});
            skLineSegment(sketch, "E2.5.2.1", {"start": v(-8.23, -195.37) * mm, "end": v(11.03, -195.37) * mm});
            skLineSegment(sketch, "E2.5.2.2", {"start": v(-8.23, -176.12) * mm, "end": v(-8.23, -195.37) * mm});
            skLineSegment(sketch, "E2.5.2.3", {"start": v(11.03, -176.12) * mm, "end": v(11.03, -195.37) * mm});
            skLineSegment(sketch, "E2.5.3.0", {"start": v(-8.23, -154.48) * mm, "end": v(11.03, -154.48) * mm});
            skLineSegment(sketch, "E2.5.3.1", {"start": v(-8.23, -173.73) * mm, "end": v(11.03, -173.73) * mm});
            skLineSegment(sketch, "E2.5.3.2", {"start": v(-8.23, -154.48) * mm, "end": v(-8.23, -173.73) * mm});
            skLineSegment(sketch, "E2.5.3.3", {"start": v(11.03, -154.48) * mm, "end": v(11.03, -173.73) * mm});
            skLineSegment(sketch, "E2.5.4.0", {"start": v(-8.23, -132.84) * mm, "end": v(11.03, -132.84) * mm});
            skLineSegment(sketch, "E2.5.4.1", {"start": v(-8.23, -152.09) * mm, "end": v(11.03, -152.09) * mm});
            skLineSegment(sketch, "E2.5.4.2", {"start": v(-8.23, -132.84) * mm, "end": v(-8.23, -152.09) * mm});
            skLineSegment(sketch, "E2.5.4.3", {"start": v(11.03, -132.84) * mm, "end": v(11.03, -152.09) * mm});
            skLineSegment(sketch, "E2.5.5.0", {"start": v(-8.23, -111.2) * mm, "end": v(11.03, -111.2) * mm});
            skLineSegment(sketch, "E2.5.5.1", {"start": v(-8.23, -130.45) * mm, "end": v(11.03, -130.45) * mm});
            skLineSegment(sketch, "E2.5.5.2", {"start": v(-8.23, -111.2) * mm, "end": v(-8.23, -130.45) * mm});
            skLineSegment(sketch, "E2.5.5.3", {"start": v(11.03, -111.2) * mm, "end": v(11.03, -130.45) * mm});
            skLineSegment(sketch, "E2.5.6.0", {"start": v(-8.23, -89.55) * mm, "end": v(11.03, -89.55) * mm});
            skLineSegment(sketch, "E2.5.6.1", {"start": v(-8.23, -108.8) * mm, "end": v(11.03, -108.8) * mm});
            skLineSegment(sketch, "E2.5.6.2", {"start": v(-8.23, -89.55) * mm, "end": v(-8.23, -108.8) * mm});
            skLineSegment(sketch, "E2.5.6.3", {"start": v(11.03, -89.55) * mm, "end": v(11.03, -108.8) * mm});
            skLineSegment(sketch, "E2.5.7.0", {"start": v(-8.23, -67.91) * mm, "end": v(11.03, -67.91) * mm});
            skLineSegment(sketch, "E2.5.7.1", {"start": v(-8.23, -87.17) * mm, "end": v(11.03, -87.17) * mm});
            skLineSegment(sketch, "E2.5.7.2", {"start": v(-8.23, -67.91) * mm, "end": v(-8.23, -87.17) * mm});
            skLineSegment(sketch, "E2.5.7.3", {"start": v(11.03, -67.91) * mm, "end": v(11.03, -87.17) * mm});
            skLineSegment(sketch, "E2.5.8.0", {"start": v(-8.23, -46.27) * mm, "end": v(11.03, -46.27) * mm});
            skLineSegment(sketch, "E2.5.8.1", {"start": v(-8.23, -65.53) * mm, "end": v(11.03, -65.53) * mm});
            skLineSegment(sketch, "E2.5.8.2", {"start": v(-8.23, -46.27) * mm, "end": v(-8.23, -65.53) * mm});
            skLineSegment(sketch, "E2.5.8.3", {"start": v(11.03, -46.27) * mm, "end": v(11.03, -65.53) * mm});
            skLineSegment(sketch, "E2.5.9.0", {"start": v(-8.23, -24.63) * mm, "end": v(11.03, -24.63) * mm});
            skLineSegment(sketch, "E2.5.9.1", {"start": v(-8.23, -43.88) * mm, "end": v(11.03, -43.88) * mm});
            skLineSegment(sketch, "E2.5.9.2", {"start": v(-8.23, -24.63) * mm, "end": v(-8.23, -43.88) * mm});
            skLineSegment(sketch, "E2.5.9.3", {"start": v(11.03, -24.63) * mm, "end": v(11.03, -43.88) * mm});
            skLineSegment(sketch, "E2.5.10.0", {"start": v(-8.23, -3) * mm, "end": v(11.03, -3) * mm});
            skLineSegment(sketch, "E2.5.10.1", {"start": v(-8.23, -22.24) * mm, "end": v(11.03, -22.24) * mm});
            skLineSegment(sketch, "E2.5.10.2", {"start": v(-8.23, -3) * mm, "end": v(-8.23, -22.24) * mm});
            skLineSegment(sketch, "E2.5.10.3", {"start": v(11.03, -3) * mm, "end": v(11.03, -22.24) * mm});
            skLineSegment(sketch, "E2.5.11.0", {"start": v(-8.23, 18.65) * mm, "end": v(11.03, 18.65) * mm});
            skLineSegment(sketch, "E2.5.11.1", {"start": v(-8.23, -0.6) * mm, "end": v(11.03, -0.6) * mm});
            skLineSegment(sketch, "E2.5.11.2", {"start": v(-8.23, 18.65) * mm, "end": v(-8.23, -0.6) * mm});
            skLineSegment(sketch, "E2.5.11.3", {"start": v(11.03, 18.65) * mm, "end": v(11.03, -0.6) * mm});
            skLineSegment(sketch, "E2.5.12.0", {"start": v(-8.23, 40.3) * mm, "end": v(11.03, 40.3) * mm});
            skLineSegment(sketch, "E2.5.12.1", {"start": v(-8.23, 21.04) * mm, "end": v(11.03, 21.04) * mm});
            skLineSegment(sketch, "E2.5.12.2", {"start": v(-8.23, 40.3) * mm, "end": v(-8.23, 21.04) * mm});
            skLineSegment(sketch, "E2.5.12.3", {"start": v(11.03, 40.3) * mm, "end": v(11.03, 21.04) * mm});
            skLineSegment(sketch, "E2.5.13.0", {"start": v(-8.23, 61.93) * mm, "end": v(11.03, 61.93) * mm});
            skLineSegment(sketch, "E2.5.13.1", {"start": v(-8.23, 42.68) * mm, "end": v(11.03, 42.68) * mm});
            skLineSegment(sketch, "E2.5.13.2", {"start": v(-8.23, 61.93) * mm, "end": v(-8.23, 42.68) * mm});
            skLineSegment(sketch, "E2.5.13.3", {"start": v(11.03, 61.93) * mm, "end": v(11.03, 42.68) * mm});
            skLineSegment(sketch, "E2.5.14.0", {"start": v(-8.23, 83.57) * mm, "end": v(11.03, 83.57) * mm});
            skLineSegment(sketch, "E2.5.14.1", {"start": v(-8.23, 64.32) * mm, "end": v(11.03, 64.32) * mm});
            skLineSegment(sketch, "E2.5.14.2", {"start": v(-8.23, 83.57) * mm, "end": v(-8.23, 64.32) * mm});
            skLineSegment(sketch, "E2.5.14.3", {"start": v(11.03, 83.57) * mm, "end": v(11.03, 64.32) * mm});
            skLineSegment(sketch, "E2.5.15.0", {"start": v(-8.23, 105.21) * mm, "end": v(11.03, 105.21) * mm});
            skLineSegment(sketch, "E2.5.15.1", {"start": v(-8.23, 85.96) * mm, "end": v(11.03, 85.96) * mm});
            skLineSegment(sketch, "E2.5.15.2", {"start": v(-8.23, 105.21) * mm, "end": v(-8.23, 85.96) * mm});
            skLineSegment(sketch, "E2.5.15.3", {"start": v(11.03, 105.21) * mm, "end": v(11.03, 85.96) * mm});
            skLineSegment(sketch, "E2.5.16.0", {"start": v(-8.23, 126.85) * mm, "end": v(11.03, 126.85) * mm});
            skLineSegment(sketch, "E2.5.16.1", {"start": v(-8.23, 107.6) * mm, "end": v(11.03, 107.6) * mm});
            skLineSegment(sketch, "E2.5.16.2", {"start": v(-8.23, 126.85) * mm, "end": v(-8.23, 107.6) * mm});
            skLineSegment(sketch, "E2.5.16.3", {"start": v(11.03, 126.85) * mm, "end": v(11.03, 107.6) * mm});
            skLineSegment(sketch, "E2.5.17.0", {"start": v(-8.23, 148.5) * mm, "end": v(11.03, 148.5) * mm});
            skLineSegment(sketch, "E2.5.17.1", {"start": v(-8.23, 129.24) * mm, "end": v(11.03, 129.24) * mm});
            skLineSegment(sketch, "E2.5.17.2", {"start": v(-8.23, 148.5) * mm, "end": v(-8.23, 129.24) * mm});
            skLineSegment(sketch, "E2.5.17.3", {"start": v(11.03, 148.5) * mm, "end": v(11.03, 129.24) * mm});
            skLineSegment(sketch, "E2.5.18.0", {"start": v(-8.23, 170.14) * mm, "end": v(11.03, 170.14) * mm});
            skLineSegment(sketch, "E2.5.18.1", {"start": v(-8.23, 150.88) * mm, "end": v(11.03, 150.88) * mm});
            skLineSegment(sketch, "E2.5.18.2", {"start": v(-8.23, 170.14) * mm, "end": v(-8.23, 150.88) * mm});
            skLineSegment(sketch, "E2.5.18.3", {"start": v(11.03, 170.14) * mm, "end": v(11.03, 150.88) * mm});
            skLineSegment(sketch, "E2.5.19.0", {"start": v(-8.23, 191.78) * mm, "end": v(11.03, 191.78) * mm});
            skLineSegment(sketch, "E2.5.19.1", {"start": v(-8.23, 172.52) * mm, "end": v(11.03, 172.52) * mm});
            skLineSegment(sketch, "E2.5.19.2", {"start": v(-8.23, 191.78) * mm, "end": v(-8.23, 172.52) * mm});
            skLineSegment(sketch, "E2.5.19.3", {"start": v(11.03, 191.78) * mm, "end": v(11.03, 172.52) * mm});
            skLineSegment(sketch, "E2.5.20.0", {"start": v(-8.23, 213.42) * mm, "end": v(11.03, 213.42) * mm});
            skLineSegment(sketch, "E2.5.20.1", {"start": v(-8.23, 194.16) * mm, "end": v(11.03, 194.16) * mm});
            skLineSegment(sketch, "E2.5.20.2", {"start": v(-8.23, 213.42) * mm, "end": v(-8.23, 194.16) * mm});
            skLineSegment(sketch, "E2.5.20.3", {"start": v(11.03, 213.42) * mm, "end": v(11.03, 194.16) * mm});
            skLineSegment(sketch, "E2.5.21.0", {"start": v(-8.23, 235.06) * mm, "end": v(11.03, 235.06) * mm});
            skLineSegment(sketch, "E2.5.21.1", {"start": v(-8.23, 215.8) * mm, "end": v(11.03, 215.8) * mm});
            skLineSegment(sketch, "E2.5.21.2", {"start": v(-8.23, 235.06) * mm, "end": v(-8.23, 215.8) * mm});
            skLineSegment(sketch, "E2.5.21.3", {"start": v(11.03, 235.06) * mm, "end": v(11.03, 215.8) * mm});
            skLineSegment(sketch, "E2.5.22.0", {"start": v(-8.23, 256.7) * mm, "end": v(11.03, 256.7) * mm});
            skLineSegment(sketch, "E2.5.22.1", {"start": v(-8.23, 237.45) * mm, "end": v(11.03, 237.45) * mm});
            skLineSegment(sketch, "E2.5.22.2", {"start": v(-8.23, 256.7) * mm, "end": v(-8.23, 237.45) * mm});
            skLineSegment(sketch, "E2.5.22.3", {"start": v(11.03, 256.7) * mm, "end": v(11.03, 237.45) * mm});
            skLineSegment(sketch, "E2.5.23.0", {"start": v(-8.23, 278.34) * mm, "end": v(11.03, 278.34) * mm});
            skLineSegment(sketch, "E2.5.23.1", {"start": v(-8.23, 259.09) * mm, "end": v(11.03, 259.09) * mm});
            skLineSegment(sketch, "E2.5.23.2", {"start": v(-8.23, 278.34) * mm, "end": v(-8.23, 259.09) * mm});
            skLineSegment(sketch, "E2.5.23.3", {"start": v(11.03, 278.34) * mm, "end": v(11.03, 259.09) * mm});
            skLineSegment(sketch, "E2.6.0.0", {"start": v(13.42, -219.4) * mm, "end": v(32.67, -219.4) * mm});
            skLineSegment(sketch, "E2.6.0.1", {"start": v(13.42, -238.65) * mm, "end": v(32.67, -238.65) * mm});
            skLineSegment(sketch, "E2.6.0.2", {"start": v(13.42, -219.4) * mm, "end": v(13.42, -238.65) * mm});
            skLineSegment(sketch, "E2.6.0.3", {"start": v(32.67, -219.4) * mm, "end": v(32.67, -238.65) * mm});
            skLineSegment(sketch, "E2.6.1.0", {"start": v(13.42, -197.76) * mm, "end": v(32.67, -197.76) * mm});
            skLineSegment(sketch, "E2.6.1.1", {"start": v(13.42, -217.01) * mm, "end": v(32.67, -217.01) * mm});
            skLineSegment(sketch, "E2.6.1.2", {"start": v(13.42, -197.76) * mm, "end": v(13.42, -217.01) * mm});
            skLineSegment(sketch, "E2.6.1.3", {"start": v(32.67, -197.76) * mm, "end": v(32.67, -217.01) * mm});
            skLineSegment(sketch, "E2.6.2.0", {"start": v(13.42, -176.12) * mm, "end": v(32.67, -176.12) * mm});
            skLineSegment(sketch, "E2.6.2.1", {"start": v(13.42, -195.37) * mm, "end": v(32.67, -195.37) * mm});
            skLineSegment(sketch, "E2.6.2.2", {"start": v(13.42, -176.12) * mm, "end": v(13.42, -195.37) * mm});
            skLineSegment(sketch, "E2.6.2.3", {"start": v(32.67, -176.12) * mm, "end": v(32.67, -195.37) * mm});
            skLineSegment(sketch, "E2.6.3.0", {"start": v(13.42, -154.48) * mm, "end": v(32.67, -154.48) * mm});
            skLineSegment(sketch, "E2.6.3.1", {"start": v(13.42, -173.73) * mm, "end": v(32.67, -173.73) * mm});
            skLineSegment(sketch, "E2.6.3.2", {"start": v(13.42, -154.48) * mm, "end": v(13.42, -173.73) * mm});
            skLineSegment(sketch, "E2.6.3.3", {"start": v(32.67, -154.48) * mm, "end": v(32.67, -173.73) * mm});
            skLineSegment(sketch, "E2.6.4.0", {"start": v(13.42, -132.84) * mm, "end": v(32.67, -132.84) * mm});
            skLineSegment(sketch, "E2.6.4.1", {"start": v(13.42, -152.09) * mm, "end": v(32.67, -152.09) * mm});
            skLineSegment(sketch, "E2.6.4.2", {"start": v(13.42, -132.84) * mm, "end": v(13.42, -152.09) * mm});
            skLineSegment(sketch, "E2.6.4.3", {"start": v(32.67, -132.84) * mm, "end": v(32.67, -152.09) * mm});
            skLineSegment(sketch, "E2.6.5.0", {"start": v(13.42, -111.2) * mm, "end": v(32.67, -111.2) * mm});
            skLineSegment(sketch, "E2.6.5.1", {"start": v(13.42, -130.45) * mm, "end": v(32.67, -130.45) * mm});
            skLineSegment(sketch, "E2.6.5.2", {"start": v(13.42, -111.2) * mm, "end": v(13.42, -130.45) * mm});
            skLineSegment(sketch, "E2.6.5.3", {"start": v(32.67, -111.2) * mm, "end": v(32.67, -130.45) * mm});
            skLineSegment(sketch, "E2.6.6.0", {"start": v(13.42, -89.55) * mm, "end": v(32.67, -89.55) * mm});
            skLineSegment(sketch, "E2.6.6.1", {"start": v(13.42, -108.8) * mm, "end": v(32.67, -108.8) * mm});
            skLineSegment(sketch, "E2.6.6.2", {"start": v(13.42, -89.55) * mm, "end": v(13.42, -108.8) * mm});
            skLineSegment(sketch, "E2.6.6.3", {"start": v(32.67, -89.55) * mm, "end": v(32.67, -108.8) * mm});
            skLineSegment(sketch, "E2.6.7.0", {"start": v(13.42, -67.91) * mm, "end": v(32.67, -67.91) * mm});
            skLineSegment(sketch, "E2.6.7.1", {"start": v(13.42, -87.17) * mm, "end": v(32.67, -87.17) * mm});
            skLineSegment(sketch, "E2.6.7.2", {"start": v(13.42, -67.91) * mm, "end": v(13.42, -87.17) * mm});
            skLineSegment(sketch, "E2.6.7.3", {"start": v(32.67, -67.91) * mm, "end": v(32.67, -87.17) * mm});
            skLineSegment(sketch, "E2.6.8.0", {"start": v(13.42, -46.27) * mm, "end": v(32.67, -46.27) * mm});
            skLineSegment(sketch, "E2.6.8.1", {"start": v(13.42, -65.53) * mm, "end": v(32.67, -65.53) * mm});
            skLineSegment(sketch, "E2.6.8.2", {"start": v(13.42, -46.27) * mm, "end": v(13.42, -65.53) * mm});
            skLineSegment(sketch, "E2.6.8.3", {"start": v(32.67, -46.27) * mm, "end": v(32.67, -65.53) * mm});
            skLineSegment(sketch, "E2.6.9.0", {"start": v(13.42, -24.63) * mm, "end": v(32.67, -24.63) * mm});
            skLineSegment(sketch, "E2.6.9.1", {"start": v(13.42, -43.88) * mm, "end": v(32.67, -43.88) * mm});
            skLineSegment(sketch, "E2.6.9.2", {"start": v(13.42, -24.63) * mm, "end": v(13.42, -43.88) * mm});
            skLineSegment(sketch, "E2.6.9.3", {"start": v(32.67, -24.63) * mm, "end": v(32.67, -43.88) * mm});
            skLineSegment(sketch, "E2.6.10.0", {"start": v(13.42, -3) * mm, "end": v(32.67, -3) * mm});
            skLineSegment(sketch, "E2.6.10.1", {"start": v(13.42, -22.24) * mm, "end": v(32.67, -22.24) * mm});
            skLineSegment(sketch, "E2.6.10.2", {"start": v(13.42, -3) * mm, "end": v(13.42, -22.24) * mm});
            skLineSegment(sketch, "E2.6.10.3", {"start": v(32.67, -3) * mm, "end": v(32.67, -22.24) * mm});
            skLineSegment(sketch, "E2.6.11.0", {"start": v(13.42, 18.65) * mm, "end": v(32.67, 18.65) * mm});
            skLineSegment(sketch, "E2.6.11.1", {"start": v(13.42, -0.6) * mm, "end": v(32.67, -0.6) * mm});
            skLineSegment(sketch, "E2.6.11.2", {"start": v(13.42, 18.65) * mm, "end": v(13.42, -0.6) * mm});
            skLineSegment(sketch, "E2.6.11.3", {"start": v(32.67, 18.65) * mm, "end": v(32.67, -0.6) * mm});
            skLineSegment(sketch, "E2.6.12.0", {"start": v(13.42, 40.3) * mm, "end": v(32.67, 40.3) * mm});
            skLineSegment(sketch, "E2.6.12.1", {"start": v(13.42, 21.04) * mm, "end": v(32.67, 21.04) * mm});
            skLineSegment(sketch, "E2.6.12.2", {"start": v(13.42, 40.3) * mm, "end": v(13.42, 21.04) * mm});
            skLineSegment(sketch, "E2.6.12.3", {"start": v(32.67, 40.3) * mm, "end": v(32.67, 21.04) * mm});
            skLineSegment(sketch, "E2.6.13.0", {"start": v(13.42, 61.93) * mm, "end": v(32.67, 61.93) * mm});
            skLineSegment(sketch, "E2.6.13.1", {"start": v(13.42, 42.68) * mm, "end": v(32.67, 42.68) * mm});
            skLineSegment(sketch, "E2.6.13.2", {"start": v(13.42, 61.93) * mm, "end": v(13.42, 42.68) * mm});
            skLineSegment(sketch, "E2.6.13.3", {"start": v(32.67, 61.93) * mm, "end": v(32.67, 42.68) * mm});
            skLineSegment(sketch, "E2.6.14.0", {"start": v(13.42, 83.57) * mm, "end": v(32.67, 83.57) * mm});
            skLineSegment(sketch, "E2.6.14.1", {"start": v(13.42, 64.32) * mm, "end": v(32.67, 64.32) * mm});
            skLineSegment(sketch, "E2.6.14.2", {"start": v(13.42, 83.57) * mm, "end": v(13.42, 64.32) * mm});
            skLineSegment(sketch, "E2.6.14.3", {"start": v(32.67, 83.57) * mm, "end": v(32.67, 64.32) * mm});
            skLineSegment(sketch, "E2.6.15.0", {"start": v(13.42, 105.21) * mm, "end": v(32.67, 105.21) * mm});
            skLineSegment(sketch, "E2.6.15.1", {"start": v(13.42, 85.96) * mm, "end": v(32.67, 85.96) * mm});
            skLineSegment(sketch, "E2.6.15.2", {"start": v(13.42, 105.21) * mm, "end": v(13.42, 85.96) * mm});
            skLineSegment(sketch, "E2.6.15.3", {"start": v(32.67, 105.21) * mm, "end": v(32.67, 85.96) * mm});
            skLineSegment(sketch, "E2.6.16.0", {"start": v(13.42, 126.85) * mm, "end": v(32.67, 126.85) * mm});
            skLineSegment(sketch, "E2.6.16.1", {"start": v(13.42, 107.6) * mm, "end": v(32.67, 107.6) * mm});
            skLineSegment(sketch, "E2.6.16.2", {"start": v(13.42, 126.85) * mm, "end": v(13.42, 107.6) * mm});
            skLineSegment(sketch, "E2.6.16.3", {"start": v(32.67, 126.85) * mm, "end": v(32.67, 107.6) * mm});
            skLineSegment(sketch, "E2.6.17.0", {"start": v(13.42, 148.5) * mm, "end": v(32.67, 148.5) * mm});
            skLineSegment(sketch, "E2.6.17.1", {"start": v(13.42, 129.24) * mm, "end": v(32.67, 129.24) * mm});
            skLineSegment(sketch, "E2.6.17.2", {"start": v(13.42, 148.5) * mm, "end": v(13.42, 129.24) * mm});
            skLineSegment(sketch, "E2.6.17.3", {"start": v(32.67, 148.5) * mm, "end": v(32.67, 129.24) * mm});
            skLineSegment(sketch, "E2.6.18.0", {"start": v(13.42, 170.14) * mm, "end": v(32.67, 170.14) * mm});
            skLineSegment(sketch, "E2.6.18.1", {"start": v(13.42, 150.88) * mm, "end": v(32.67, 150.88) * mm});
            skLineSegment(sketch, "E2.6.18.2", {"start": v(13.42, 170.14) * mm, "end": v(13.42, 150.88) * mm});
            skLineSegment(sketch, "E2.6.18.3", {"start": v(32.67, 170.14) * mm, "end": v(32.67, 150.88) * mm});
            skLineSegment(sketch, "E2.6.19.0", {"start": v(13.42, 191.78) * mm, "end": v(32.67, 191.78) * mm});
            skLineSegment(sketch, "E2.6.19.1", {"start": v(13.42, 172.52) * mm, "end": v(32.67, 172.52) * mm});
            skLineSegment(sketch, "E2.6.19.2", {"start": v(13.42, 191.78) * mm, "end": v(13.42, 172.52) * mm});
            skLineSegment(sketch, "E2.6.19.3", {"start": v(32.67, 191.78) * mm, "end": v(32.67, 172.52) * mm});
            skLineSegment(sketch, "E2.6.20.0", {"start": v(13.42, 213.42) * mm, "end": v(32.67, 213.42) * mm});
            skLineSegment(sketch, "E2.6.20.1", {"start": v(13.42, 194.16) * mm, "end": v(32.67, 194.16) * mm});
            skLineSegment(sketch, "E2.6.20.2", {"start": v(13.42, 213.42) * mm, "end": v(13.42, 194.16) * mm});
            skLineSegment(sketch, "E2.6.20.3", {"start": v(32.67, 213.42) * mm, "end": v(32.67, 194.16) * mm});
            skLineSegment(sketch, "E2.6.21.0", {"start": v(13.42, 235.06) * mm, "end": v(32.67, 235.06) * mm});
            skLineSegment(sketch, "E2.6.21.1", {"start": v(13.42, 215.8) * mm, "end": v(32.67, 215.8) * mm});
            skLineSegment(sketch, "E2.6.21.2", {"start": v(13.42, 235.06) * mm, "end": v(13.42, 215.8) * mm});
            skLineSegment(sketch, "E2.6.21.3", {"start": v(32.67, 235.06) * mm, "end": v(32.67, 215.8) * mm});
            skLineSegment(sketch, "E2.6.22.0", {"start": v(13.42, 256.7) * mm, "end": v(32.67, 256.7) * mm});
            skLineSegment(sketch, "E2.6.22.1", {"start": v(13.42, 237.45) * mm, "end": v(32.67, 237.45) * mm});
            skLineSegment(sketch, "E2.6.22.2", {"start": v(13.42, 256.7) * mm, "end": v(13.42, 237.45) * mm});
            skLineSegment(sketch, "E2.6.22.3", {"start": v(32.67, 256.7) * mm, "end": v(32.67, 237.45) * mm});
            skLineSegment(sketch, "E2.6.23.0", {"start": v(13.42, 278.34) * mm, "end": v(32.67, 278.34) * mm});
            skLineSegment(sketch, "E2.6.23.1", {"start": v(13.42, 259.09) * mm, "end": v(32.67, 259.09) * mm});
            skLineSegment(sketch, "E2.6.23.2", {"start": v(13.42, 278.34) * mm, "end": v(13.42, 259.09) * mm});
            skLineSegment(sketch, "E2.6.23.3", {"start": v(32.67, 278.34) * mm, "end": v(32.67, 259.09) * mm});
            skLineSegment(sketch, "E2.7.0.0", {"start": v(35.06, -219.4) * mm, "end": v(54.3, -219.4) * mm});
            skLineSegment(sketch, "E2.7.0.1", {"start": v(35.06, -238.65) * mm, "end": v(54.3, -238.65) * mm});
            skLineSegment(sketch, "E2.7.0.2", {"start": v(35.06, -219.4) * mm, "end": v(35.06, -238.65) * mm});
            skLineSegment(sketch, "E2.7.0.3", {"start": v(54.3, -219.4) * mm, "end": v(54.3, -238.65) * mm});
            skLineSegment(sketch, "E2.7.1.0", {"start": v(35.06, -197.76) * mm, "end": v(54.3, -197.76) * mm});
            skLineSegment(sketch, "E2.7.1.1", {"start": v(35.06, -217.01) * mm, "end": v(54.3, -217.01) * mm});
            skLineSegment(sketch, "E2.7.1.2", {"start": v(35.06, -197.76) * mm, "end": v(35.06, -217.01) * mm});
            skLineSegment(sketch, "E2.7.1.3", {"start": v(54.3, -197.76) * mm, "end": v(54.3, -217.01) * mm});
            skLineSegment(sketch, "E2.7.2.0", {"start": v(35.06, -176.12) * mm, "end": v(54.3, -176.12) * mm});
            skLineSegment(sketch, "E2.7.2.1", {"start": v(35.06, -195.37) * mm, "end": v(54.3, -195.37) * mm});
            skLineSegment(sketch, "E2.7.2.2", {"start": v(35.06, -176.12) * mm, "end": v(35.06, -195.37) * mm});
            skLineSegment(sketch, "E2.7.2.3", {"start": v(54.3, -176.12) * mm, "end": v(54.3, -195.37) * mm});
            skLineSegment(sketch, "E2.7.3.0", {"start": v(35.06, -154.48) * mm, "end": v(54.3, -154.48) * mm});
            skLineSegment(sketch, "E2.7.3.1", {"start": v(35.06, -173.73) * mm, "end": v(54.3, -173.73) * mm});
            skLineSegment(sketch, "E2.7.3.2", {"start": v(35.06, -154.48) * mm, "end": v(35.06, -173.73) * mm});
            skLineSegment(sketch, "E2.7.3.3", {"start": v(54.3, -154.48) * mm, "end": v(54.3, -173.73) * mm});
            skLineSegment(sketch, "E2.7.4.0", {"start": v(35.06, -132.84) * mm, "end": v(54.3, -132.84) * mm});
            skLineSegment(sketch, "E2.7.4.1", {"start": v(35.06, -152.09) * mm, "end": v(54.3, -152.09) * mm});
            skLineSegment(sketch, "E2.7.4.2", {"start": v(35.06, -132.84) * mm, "end": v(35.06, -152.09) * mm});
            skLineSegment(sketch, "E2.7.4.3", {"start": v(54.3, -132.84) * mm, "end": v(54.3, -152.09) * mm});
            skLineSegment(sketch, "E2.7.5.0", {"start": v(35.06, -111.2) * mm, "end": v(54.3, -111.2) * mm});
            skLineSegment(sketch, "E2.7.5.1", {"start": v(35.06, -130.45) * mm, "end": v(54.3, -130.45) * mm});
            skLineSegment(sketch, "E2.7.5.2", {"start": v(35.06, -111.2) * mm, "end": v(35.06, -130.45) * mm});
            skLineSegment(sketch, "E2.7.5.3", {"start": v(54.3, -111.2) * mm, "end": v(54.3, -130.45) * mm});
            skLineSegment(sketch, "E2.7.6.0", {"start": v(35.06, -89.55) * mm, "end": v(54.3, -89.55) * mm});
            skLineSegment(sketch, "E2.7.6.1", {"start": v(35.06, -108.8) * mm, "end": v(54.3, -108.8) * mm});
            skLineSegment(sketch, "E2.7.6.2", {"start": v(35.06, -89.55) * mm, "end": v(35.06, -108.8) * mm});
            skLineSegment(sketch, "E2.7.6.3", {"start": v(54.3, -89.55) * mm, "end": v(54.3, -108.8) * mm});
            skLineSegment(sketch, "E2.7.7.0", {"start": v(35.06, -67.91) * mm, "end": v(54.3, -67.91) * mm});
            skLineSegment(sketch, "E2.7.7.1", {"start": v(35.06, -87.17) * mm, "end": v(54.3, -87.17) * mm});
            skLineSegment(sketch, "E2.7.7.2", {"start": v(35.06, -67.91) * mm, "end": v(35.06, -87.17) * mm});
            skLineSegment(sketch, "E2.7.7.3", {"start": v(54.3, -67.91) * mm, "end": v(54.3, -87.17) * mm});
            skLineSegment(sketch, "E2.7.8.0", {"start": v(35.06, -46.27) * mm, "end": v(54.3, -46.27) * mm});
            skLineSegment(sketch, "E2.7.8.1", {"start": v(35.06, -65.53) * mm, "end": v(54.3, -65.53) * mm});
            skLineSegment(sketch, "E2.7.8.2", {"start": v(35.06, -46.27) * mm, "end": v(35.06, -65.53) * mm});
            skLineSegment(sketch, "E2.7.8.3", {"start": v(54.3, -46.27) * mm, "end": v(54.3, -65.53) * mm});
            skLineSegment(sketch, "E2.7.9.0", {"start": v(35.06, -24.63) * mm, "end": v(54.3, -24.63) * mm});
            skLineSegment(sketch, "E2.7.9.1", {"start": v(35.06, -43.88) * mm, "end": v(54.3, -43.88) * mm});
            skLineSegment(sketch, "E2.7.9.2", {"start": v(35.06, -24.63) * mm, "end": v(35.06, -43.88) * mm});
            skLineSegment(sketch, "E2.7.9.3", {"start": v(54.3, -24.63) * mm, "end": v(54.3, -43.88) * mm});
            skLineSegment(sketch, "E2.7.10.0", {"start": v(35.06, -3) * mm, "end": v(54.3, -3) * mm});
            skLineSegment(sketch, "E2.7.10.1", {"start": v(35.06, -22.24) * mm, "end": v(54.3, -22.24) * mm});
            skLineSegment(sketch, "E2.7.10.2", {"start": v(35.06, -3) * mm, "end": v(35.06, -22.24) * mm});
            skLineSegment(sketch, "E2.7.10.3", {"start": v(54.3, -3) * mm, "end": v(54.3, -22.24) * mm});
            skLineSegment(sketch, "E2.7.11.0", {"start": v(35.06, 18.65) * mm, "end": v(54.3, 18.65) * mm});
            skLineSegment(sketch, "E2.7.11.1", {"start": v(35.06, -0.6) * mm, "end": v(54.3, -0.6) * mm});
            skLineSegment(sketch, "E2.7.11.2", {"start": v(35.06, 18.65) * mm, "end": v(35.06, -0.6) * mm});
            skLineSegment(sketch, "E2.7.11.3", {"start": v(54.3, 18.65) * mm, "end": v(54.3, -0.6) * mm});
            skLineSegment(sketch, "E2.7.12.0", {"start": v(35.06, 40.3) * mm, "end": v(54.3, 40.3) * mm});
            skLineSegment(sketch, "E2.7.12.1", {"start": v(35.06, 21.04) * mm, "end": v(54.3, 21.04) * mm});
            skLineSegment(sketch, "E2.7.12.2", {"start": v(35.06, 40.3) * mm, "end": v(35.06, 21.04) * mm});
            skLineSegment(sketch, "E2.7.12.3", {"start": v(54.3, 40.3) * mm, "end": v(54.3, 21.04) * mm});
            skLineSegment(sketch, "E2.7.13.0", {"start": v(35.06, 61.93) * mm, "end": v(54.3, 61.93) * mm});
            skLineSegment(sketch, "E2.7.13.1", {"start": v(35.06, 42.68) * mm, "end": v(54.3, 42.68) * mm});
            skLineSegment(sketch, "E2.7.13.2", {"start": v(35.06, 61.93) * mm, "end": v(35.06, 42.68) * mm});
            skLineSegment(sketch, "E2.7.13.3", {"start": v(54.3, 61.93) * mm, "end": v(54.3, 42.68) * mm});
            skLineSegment(sketch, "E2.7.14.0", {"start": v(35.06, 83.57) * mm, "end": v(54.3, 83.57) * mm});
            skLineSegment(sketch, "E2.7.14.1", {"start": v(35.06, 64.32) * mm, "end": v(54.3, 64.32) * mm});
            skLineSegment(sketch, "E2.7.14.2", {"start": v(35.06, 83.57) * mm, "end": v(35.06, 64.32) * mm});
            skLineSegment(sketch, "E2.7.14.3", {"start": v(54.3, 83.57) * mm, "end": v(54.3, 64.32) * mm});
            skLineSegment(sketch, "E2.7.15.0", {"start": v(35.06, 105.21) * mm, "end": v(54.3, 105.21) * mm});
            skLineSegment(sketch, "E2.7.15.1", {"start": v(35.06, 85.96) * mm, "end": v(54.3, 85.96) * mm});
            skLineSegment(sketch, "E2.7.15.2", {"start": v(35.06, 105.21) * mm, "end": v(35.06, 85.96) * mm});
            skLineSegment(sketch, "E2.7.15.3", {"start": v(54.3, 105.21) * mm, "end": v(54.3, 85.96) * mm});
            skLineSegment(sketch, "E2.7.16.0", {"start": v(35.06, 126.85) * mm, "end": v(54.3, 126.85) * mm});
            skLineSegment(sketch, "E2.7.16.1", {"start": v(35.06, 107.6) * mm, "end": v(54.3, 107.6) * mm});
            skLineSegment(sketch, "E2.7.16.2", {"start": v(35.06, 126.85) * mm, "end": v(35.06, 107.6) * mm});
            skLineSegment(sketch, "E2.7.16.3", {"start": v(54.3, 126.85) * mm, "end": v(54.3, 107.6) * mm});
            skLineSegment(sketch, "E2.7.17.0", {"start": v(35.06, 148.5) * mm, "end": v(54.3, 148.5) * mm});
            skLineSegment(sketch, "E2.7.17.1", {"start": v(35.06, 129.24) * mm, "end": v(54.3, 129.24) * mm});
            skLineSegment(sketch, "E2.7.17.2", {"start": v(35.06, 148.5) * mm, "end": v(35.06, 129.24) * mm});
            skLineSegment(sketch, "E2.7.17.3", {"start": v(54.3, 148.5) * mm, "end": v(54.3, 129.24) * mm});
            skLineSegment(sketch, "E2.7.18.0", {"start": v(35.06, 170.14) * mm, "end": v(54.3, 170.14) * mm});
            skLineSegment(sketch, "E2.7.18.1", {"start": v(35.06, 150.88) * mm, "end": v(54.3, 150.88) * mm});
            skLineSegment(sketch, "E2.7.18.2", {"start": v(35.06, 170.14) * mm, "end": v(35.06, 150.88) * mm});
            skLineSegment(sketch, "E2.7.18.3", {"start": v(54.3, 170.14) * mm, "end": v(54.3, 150.88) * mm});
            skLineSegment(sketch, "E2.7.19.0", {"start": v(35.06, 191.78) * mm, "end": v(54.3, 191.78) * mm});
            skLineSegment(sketch, "E2.7.19.1", {"start": v(35.06, 172.52) * mm, "end": v(54.3, 172.52) * mm});
            skLineSegment(sketch, "E2.7.19.2", {"start": v(35.06, 191.78) * mm, "end": v(35.06, 172.52) * mm});
            skLineSegment(sketch, "E2.7.19.3", {"start": v(54.3, 191.78) * mm, "end": v(54.3, 172.52) * mm});
            skLineSegment(sketch, "E2.7.20.0", {"start": v(35.06, 213.42) * mm, "end": v(54.3, 213.42) * mm});
            skLineSegment(sketch, "E2.7.20.1", {"start": v(35.06, 194.16) * mm, "end": v(54.3, 194.16) * mm});
            skLineSegment(sketch, "E2.7.20.2", {"start": v(35.06, 213.42) * mm, "end": v(35.06, 194.16) * mm});
            skLineSegment(sketch, "E2.7.20.3", {"start": v(54.3, 213.42) * mm, "end": v(54.3, 194.16) * mm});
            skLineSegment(sketch, "E2.7.21.0", {"start": v(35.06, 235.06) * mm, "end": v(54.3, 235.06) * mm});
            skLineSegment(sketch, "E2.7.21.1", {"start": v(35.06, 215.8) * mm, "end": v(54.3, 215.8) * mm});
            skLineSegment(sketch, "E2.7.21.2", {"start": v(35.06, 235.06) * mm, "end": v(35.06, 215.8) * mm});
            skLineSegment(sketch, "E2.7.21.3", {"start": v(54.3, 235.06) * mm, "end": v(54.3, 215.8) * mm});
            skLineSegment(sketch, "E2.7.22.0", {"start": v(35.06, 256.7) * mm, "end": v(54.3, 256.7) * mm});
            skLineSegment(sketch, "E2.7.22.1", {"start": v(35.06, 237.45) * mm, "end": v(54.3, 237.45) * mm});
            skLineSegment(sketch, "E2.7.22.2", {"start": v(35.06, 256.7) * mm, "end": v(35.06, 237.45) * mm});
            skLineSegment(sketch, "E2.7.22.3", {"start": v(54.3, 256.7) * mm, "end": v(54.3, 237.45) * mm});
            skLineSegment(sketch, "E2.7.23.0", {"start": v(35.06, 278.34) * mm, "end": v(54.3, 278.34) * mm});
            skLineSegment(sketch, "E2.7.23.1", {"start": v(35.06, 259.09) * mm, "end": v(54.3, 259.09) * mm});
            skLineSegment(sketch, "E2.7.23.2", {"start": v(35.06, 278.34) * mm, "end": v(35.06, 259.09) * mm});
            skLineSegment(sketch, "E2.7.23.3", {"start": v(54.3, 278.34) * mm, "end": v(54.3, 259.09) * mm});
            skLineSegment(sketch, "E2.8.0.0", {"start": v(56.7, -219.4) * mm, "end": v(75.95, -219.4) * mm});
            skLineSegment(sketch, "E2.8.0.1", {"start": v(56.7, -238.65) * mm, "end": v(75.95, -238.65) * mm});
            skLineSegment(sketch, "E2.8.0.2", {"start": v(56.7, -219.4) * mm, "end": v(56.7, -238.65) * mm});
            skLineSegment(sketch, "E2.8.0.3", {"start": v(75.95, -219.4) * mm, "end": v(75.95, -238.65) * mm});
            skLineSegment(sketch, "E2.8.1.0", {"start": v(56.7, -197.76) * mm, "end": v(75.95, -197.76) * mm});
            skLineSegment(sketch, "E2.8.1.1", {"start": v(56.7, -217.01) * mm, "end": v(75.95, -217.01) * mm});
            skLineSegment(sketch, "E2.8.1.2", {"start": v(56.7, -197.76) * mm, "end": v(56.7, -217.01) * mm});
            skLineSegment(sketch, "E2.8.1.3", {"start": v(75.95, -197.76) * mm, "end": v(75.95, -217.01) * mm});
            skLineSegment(sketch, "E2.8.2.0", {"start": v(56.7, -176.12) * mm, "end": v(75.95, -176.12) * mm});
            skLineSegment(sketch, "E2.8.2.1", {"start": v(56.7, -195.37) * mm, "end": v(75.95, -195.37) * mm});
            skLineSegment(sketch, "E2.8.2.2", {"start": v(56.7, -176.12) * mm, "end": v(56.7, -195.37) * mm});
            skLineSegment(sketch, "E2.8.2.3", {"start": v(75.95, -176.12) * mm, "end": v(75.95, -195.37) * mm});
            skLineSegment(sketch, "E2.8.3.0", {"start": v(56.7, -154.48) * mm, "end": v(75.95, -154.48) * mm});
            skLineSegment(sketch, "E2.8.3.1", {"start": v(56.7, -173.73) * mm, "end": v(75.95, -173.73) * mm});
            skLineSegment(sketch, "E2.8.3.2", {"start": v(56.7, -154.48) * mm, "end": v(56.7, -173.73) * mm});
            skLineSegment(sketch, "E2.8.3.3", {"start": v(75.95, -154.48) * mm, "end": v(75.95, -173.73) * mm});
            skLineSegment(sketch, "E2.8.4.0", {"start": v(56.7, -132.84) * mm, "end": v(75.95, -132.84) * mm});
            skLineSegment(sketch, "E2.8.4.1", {"start": v(56.7, -152.09) * mm, "end": v(75.95, -152.09) * mm});
            skLineSegment(sketch, "E2.8.4.2", {"start": v(56.7, -132.84) * mm, "end": v(56.7, -152.09) * mm});
            skLineSegment(sketch, "E2.8.4.3", {"start": v(75.95, -132.84) * mm, "end": v(75.95, -152.09) * mm});
            skLineSegment(sketch, "E2.8.5.0", {"start": v(56.7, -111.2) * mm, "end": v(75.95, -111.2) * mm});
            skLineSegment(sketch, "E2.8.5.1", {"start": v(56.7, -130.45) * mm, "end": v(75.95, -130.45) * mm});
            skLineSegment(sketch, "E2.8.5.2", {"start": v(56.7, -111.2) * mm, "end": v(56.7, -130.45) * mm});
            skLineSegment(sketch, "E2.8.5.3", {"start": v(75.95, -111.2) * mm, "end": v(75.95, -130.45) * mm});
            skLineSegment(sketch, "E2.8.6.0", {"start": v(56.7, -89.55) * mm, "end": v(75.95, -89.55) * mm});
            skLineSegment(sketch, "E2.8.6.1", {"start": v(56.7, -108.8) * mm, "end": v(75.95, -108.8) * mm});
            skLineSegment(sketch, "E2.8.6.2", {"start": v(56.7, -89.55) * mm, "end": v(56.7, -108.8) * mm});
            skLineSegment(sketch, "E2.8.6.3", {"start": v(75.95, -89.55) * mm, "end": v(75.95, -108.8) * mm});
            skLineSegment(sketch, "E2.8.7.0", {"start": v(56.7, -67.91) * mm, "end": v(75.95, -67.91) * mm});
            skLineSegment(sketch, "E2.8.7.1", {"start": v(56.7, -87.17) * mm, "end": v(75.95, -87.17) * mm});
            skLineSegment(sketch, "E2.8.7.2", {"start": v(56.7, -67.91) * mm, "end": v(56.7, -87.17) * mm});
            skLineSegment(sketch, "E2.8.7.3", {"start": v(75.95, -67.91) * mm, "end": v(75.95, -87.17) * mm});
            skLineSegment(sketch, "E2.8.8.0", {"start": v(56.7, -46.27) * mm, "end": v(75.95, -46.27) * mm});
            skLineSegment(sketch, "E2.8.8.1", {"start": v(56.7, -65.53) * mm, "end": v(75.95, -65.53) * mm});
            skLineSegment(sketch, "E2.8.8.2", {"start": v(56.7, -46.27) * mm, "end": v(56.7, -65.53) * mm});
            skLineSegment(sketch, "E2.8.8.3", {"start": v(75.95, -46.27) * mm, "end": v(75.95, -65.53) * mm});
            skLineSegment(sketch, "E2.8.9.0", {"start": v(56.7, -24.63) * mm, "end": v(75.95, -24.63) * mm});
            skLineSegment(sketch, "E2.8.9.1", {"start": v(56.7, -43.88) * mm, "end": v(75.95, -43.88) * mm});
            skLineSegment(sketch, "E2.8.9.2", {"start": v(56.7, -24.63) * mm, "end": v(56.7, -43.88) * mm});
            skLineSegment(sketch, "E2.8.9.3", {"start": v(75.95, -24.63) * mm, "end": v(75.95, -43.88) * mm});
            skLineSegment(sketch, "E2.8.10.0", {"start": v(56.7, -3) * mm, "end": v(75.95, -3) * mm});
            skLineSegment(sketch, "E2.8.10.1", {"start": v(56.7, -22.24) * mm, "end": v(75.95, -22.24) * mm});
            skLineSegment(sketch, "E2.8.10.2", {"start": v(56.7, -3) * mm, "end": v(56.7, -22.24) * mm});
            skLineSegment(sketch, "E2.8.10.3", {"start": v(75.95, -3) * mm, "end": v(75.95, -22.24) * mm});
            skLineSegment(sketch, "E2.8.11.0", {"start": v(56.7, 18.65) * mm, "end": v(75.95, 18.65) * mm});
            skLineSegment(sketch, "E2.8.11.1", {"start": v(56.7, -0.6) * mm, "end": v(75.95, -0.6) * mm});
            skLineSegment(sketch, "E2.8.11.2", {"start": v(56.7, 18.65) * mm, "end": v(56.7, -0.6) * mm});
            skLineSegment(sketch, "E2.8.11.3", {"start": v(75.95, 18.65) * mm, "end": v(75.95, -0.6) * mm});
            skLineSegment(sketch, "E2.8.12.0", {"start": v(56.7, 40.3) * mm, "end": v(75.95, 40.3) * mm});
            skLineSegment(sketch, "E2.8.12.1", {"start": v(56.7, 21.04) * mm, "end": v(75.95, 21.04) * mm});
            skLineSegment(sketch, "E2.8.12.2", {"start": v(56.7, 40.3) * mm, "end": v(56.7, 21.04) * mm});
            skLineSegment(sketch, "E2.8.12.3", {"start": v(75.95, 40.3) * mm, "end": v(75.95, 21.04) * mm});
            skLineSegment(sketch, "E2.8.13.0", {"start": v(56.7, 61.93) * mm, "end": v(75.95, 61.93) * mm});
            skLineSegment(sketch, "E2.8.13.1", {"start": v(56.7, 42.68) * mm, "end": v(75.95, 42.68) * mm});
            skLineSegment(sketch, "E2.8.13.2", {"start": v(56.7, 61.93) * mm, "end": v(56.7, 42.68) * mm});
            skLineSegment(sketch, "E2.8.13.3", {"start": v(75.95, 61.93) * mm, "end": v(75.95, 42.68) * mm});
            skLineSegment(sketch, "E2.8.14.0", {"start": v(56.7, 83.57) * mm, "end": v(75.95, 83.57) * mm});
            skLineSegment(sketch, "E2.8.14.1", {"start": v(56.7, 64.32) * mm, "end": v(75.95, 64.32) * mm});
            skLineSegment(sketch, "E2.8.14.2", {"start": v(56.7, 83.57) * mm, "end": v(56.7, 64.32) * mm});
            skLineSegment(sketch, "E2.8.14.3", {"start": v(75.95, 83.57) * mm, "end": v(75.95, 64.32) * mm});
            skLineSegment(sketch, "E2.8.15.0", {"start": v(56.7, 105.21) * mm, "end": v(75.95, 105.21) * mm});
            skLineSegment(sketch, "E2.8.15.1", {"start": v(56.7, 85.96) * mm, "end": v(75.95, 85.96) * mm});
            skLineSegment(sketch, "E2.8.15.2", {"start": v(56.7, 105.21) * mm, "end": v(56.7, 85.96) * mm});
            skLineSegment(sketch, "E2.8.15.3", {"start": v(75.95, 105.21) * mm, "end": v(75.95, 85.96) * mm});
            skLineSegment(sketch, "E2.8.16.0", {"start": v(56.7, 126.85) * mm, "end": v(75.95, 126.85) * mm});
            skLineSegment(sketch, "E2.8.16.1", {"start": v(56.7, 107.6) * mm, "end": v(75.95, 107.6) * mm});
            skLineSegment(sketch, "E2.8.16.2", {"start": v(56.7, 126.85) * mm, "end": v(56.7, 107.6) * mm});
            skLineSegment(sketch, "E2.8.16.3", {"start": v(75.95, 126.85) * mm, "end": v(75.95, 107.6) * mm});
            skLineSegment(sketch, "E2.8.17.0", {"start": v(56.7, 148.5) * mm, "end": v(75.95, 148.5) * mm});
            skLineSegment(sketch, "E2.8.17.1", {"start": v(56.7, 129.24) * mm, "end": v(75.95, 129.24) * mm});
            skLineSegment(sketch, "E2.8.17.2", {"start": v(56.7, 148.5) * mm, "end": v(56.7, 129.24) * mm});
            skLineSegment(sketch, "E2.8.17.3", {"start": v(75.95, 148.5) * mm, "end": v(75.95, 129.24) * mm});
            skLineSegment(sketch, "E2.8.18.0", {"start": v(56.7, 170.14) * mm, "end": v(75.95, 170.14) * mm});
            skLineSegment(sketch, "E2.8.18.1", {"start": v(56.7, 150.88) * mm, "end": v(75.95, 150.88) * mm});
            skLineSegment(sketch, "E2.8.18.2", {"start": v(56.7, 170.14) * mm, "end": v(56.7, 150.88) * mm});
            skLineSegment(sketch, "E2.8.18.3", {"start": v(75.95, 170.14) * mm, "end": v(75.95, 150.88) * mm});
            skLineSegment(sketch, "E2.8.19.0", {"start": v(56.7, 191.78) * mm, "end": v(75.95, 191.78) * mm});
            skLineSegment(sketch, "E2.8.19.1", {"start": v(56.7, 172.52) * mm, "end": v(75.95, 172.52) * mm});
            skLineSegment(sketch, "E2.8.19.2", {"start": v(56.7, 191.78) * mm, "end": v(56.7, 172.52) * mm});
            skLineSegment(sketch, "E2.8.19.3", {"start": v(75.95, 191.78) * mm, "end": v(75.95, 172.52) * mm});
            skLineSegment(sketch, "E2.8.20.0", {"start": v(56.7, 213.42) * mm, "end": v(75.95, 213.42) * mm});
            skLineSegment(sketch, "E2.8.20.1", {"start": v(56.7, 194.16) * mm, "end": v(75.95, 194.16) * mm});
            skLineSegment(sketch, "E2.8.20.2", {"start": v(56.7, 213.42) * mm, "end": v(56.7, 194.16) * mm});
            skLineSegment(sketch, "E2.8.20.3", {"start": v(75.95, 213.42) * mm, "end": v(75.95, 194.16) * mm});
            skLineSegment(sketch, "E2.8.21.0", {"start": v(56.7, 235.06) * mm, "end": v(75.95, 235.06) * mm});
            skLineSegment(sketch, "E2.8.21.1", {"start": v(56.7, 215.8) * mm, "end": v(75.95, 215.8) * mm});
            skLineSegment(sketch, "E2.8.21.2", {"start": v(56.7, 235.06) * mm, "end": v(56.7, 215.8) * mm});
            skLineSegment(sketch, "E2.8.21.3", {"start": v(75.95, 235.06) * mm, "end": v(75.95, 215.8) * mm});
            skLineSegment(sketch, "E2.8.22.0", {"start": v(56.7, 256.7) * mm, "end": v(75.95, 256.7) * mm});
            skLineSegment(sketch, "E2.8.22.1", {"start": v(56.7, 237.45) * mm, "end": v(75.95, 237.45) * mm});
            skLineSegment(sketch, "E2.8.22.2", {"start": v(56.7, 256.7) * mm, "end": v(56.7, 237.45) * mm});
            skLineSegment(sketch, "E2.8.22.3", {"start": v(75.95, 256.7) * mm, "end": v(75.95, 237.45) * mm});
            skLineSegment(sketch, "E2.8.23.0", {"start": v(56.7, 278.34) * mm, "end": v(75.95, 278.34) * mm});
            skLineSegment(sketch, "E2.8.23.1", {"start": v(56.7, 259.09) * mm, "end": v(75.95, 259.09) * mm});
            skLineSegment(sketch, "E2.8.23.2", {"start": v(56.7, 278.34) * mm, "end": v(56.7, 259.09) * mm});
            skLineSegment(sketch, "E2.8.23.3", {"start": v(75.95, 278.34) * mm, "end": v(75.95, 259.09) * mm});
            skLineSegment(sketch, "E2.9.0.0", {"start": v(78.34, -219.4) * mm, "end": v(97.6, -219.4) * mm});
            skLineSegment(sketch, "E2.9.0.1", {"start": v(78.34, -238.65) * mm, "end": v(97.6, -238.65) * mm});
            skLineSegment(sketch, "E2.9.0.2", {"start": v(78.34, -219.4) * mm, "end": v(78.34, -238.65) * mm});
            skLineSegment(sketch, "E2.9.0.3", {"start": v(97.6, -219.4) * mm, "end": v(97.6, -238.65) * mm});
            skLineSegment(sketch, "E2.9.1.0", {"start": v(78.34, -197.76) * mm, "end": v(97.6, -197.76) * mm});
            skLineSegment(sketch, "E2.9.1.1", {"start": v(78.34, -217.01) * mm, "end": v(97.6, -217.01) * mm});
            skLineSegment(sketch, "E2.9.1.2", {"start": v(78.34, -197.76) * mm, "end": v(78.34, -217.01) * mm});
            skLineSegment(sketch, "E2.9.1.3", {"start": v(97.6, -197.76) * mm, "end": v(97.6, -217.01) * mm});
            skLineSegment(sketch, "E2.9.2.0", {"start": v(78.34, -176.12) * mm, "end": v(97.6, -176.12) * mm});
            skLineSegment(sketch, "E2.9.2.1", {"start": v(78.34, -195.37) * mm, "end": v(97.6, -195.37) * mm});
            skLineSegment(sketch, "E2.9.2.2", {"start": v(78.34, -176.12) * mm, "end": v(78.34, -195.37) * mm});
            skLineSegment(sketch, "E2.9.2.3", {"start": v(97.6, -176.12) * mm, "end": v(97.6, -195.37) * mm});
            skLineSegment(sketch, "E2.9.3.0", {"start": v(78.34, -154.48) * mm, "end": v(97.6, -154.48) * mm});
            skLineSegment(sketch, "E2.9.3.1", {"start": v(78.34, -173.73) * mm, "end": v(97.6, -173.73) * mm});
            skLineSegment(sketch, "E2.9.3.2", {"start": v(78.34, -154.48) * mm, "end": v(78.34, -173.73) * mm});
            skLineSegment(sketch, "E2.9.3.3", {"start": v(97.6, -154.48) * mm, "end": v(97.6, -173.73) * mm});
            skLineSegment(sketch, "E2.9.4.0", {"start": v(78.34, -132.84) * mm, "end": v(97.6, -132.84) * mm});
            skLineSegment(sketch, "E2.9.4.1", {"start": v(78.34, -152.09) * mm, "end": v(97.6, -152.09) * mm});
            skLineSegment(sketch, "E2.9.4.2", {"start": v(78.34, -132.84) * mm, "end": v(78.34, -152.09) * mm});
            skLineSegment(sketch, "E2.9.4.3", {"start": v(97.6, -132.84) * mm, "end": v(97.6, -152.09) * mm});
            skLineSegment(sketch, "E2.9.5.0", {"start": v(78.34, -111.2) * mm, "end": v(97.6, -111.2) * mm});
            skLineSegment(sketch, "E2.9.5.1", {"start": v(78.34, -130.45) * mm, "end": v(97.6, -130.45) * mm});
            skLineSegment(sketch, "E2.9.5.2", {"start": v(78.34, -111.2) * mm, "end": v(78.34, -130.45) * mm});
            skLineSegment(sketch, "E2.9.5.3", {"start": v(97.6, -111.2) * mm, "end": v(97.6, -130.45) * mm});
            skLineSegment(sketch, "E2.9.6.0", {"start": v(78.34, -89.55) * mm, "end": v(97.6, -89.55) * mm});
            skLineSegment(sketch, "E2.9.6.1", {"start": v(78.34, -108.8) * mm, "end": v(97.6, -108.8) * mm});
            skLineSegment(sketch, "E2.9.6.2", {"start": v(78.34, -89.55) * mm, "end": v(78.34, -108.8) * mm});
            skLineSegment(sketch, "E2.9.6.3", {"start": v(97.6, -89.55) * mm, "end": v(97.6, -108.8) * mm});
            skLineSegment(sketch, "E2.9.7.0", {"start": v(78.34, -67.91) * mm, "end": v(97.6, -67.91) * mm});
            skLineSegment(sketch, "E2.9.7.1", {"start": v(78.34, -87.17) * mm, "end": v(97.6, -87.17) * mm});
            skLineSegment(sketch, "E2.9.7.2", {"start": v(78.34, -67.91) * mm, "end": v(78.34, -87.17) * mm});
            skLineSegment(sketch, "E2.9.7.3", {"start": v(97.6, -67.91) * mm, "end": v(97.6, -87.17) * mm});
            skLineSegment(sketch, "E2.9.8.0", {"start": v(78.34, -46.27) * mm, "end": v(97.6, -46.27) * mm});
            skLineSegment(sketch, "E2.9.8.1", {"start": v(78.34, -65.53) * mm, "end": v(97.6, -65.53) * mm});
            skLineSegment(sketch, "E2.9.8.2", {"start": v(78.34, -46.27) * mm, "end": v(78.34, -65.53) * mm});
            skLineSegment(sketch, "E2.9.8.3", {"start": v(97.6, -46.27) * mm, "end": v(97.6, -65.53) * mm});
            skLineSegment(sketch, "E2.9.9.0", {"start": v(78.34, -24.63) * mm, "end": v(97.6, -24.63) * mm});
            skLineSegment(sketch, "E2.9.9.1", {"start": v(78.34, -43.88) * mm, "end": v(97.6, -43.88) * mm});
            skLineSegment(sketch, "E2.9.9.2", {"start": v(78.34, -24.63) * mm, "end": v(78.34, -43.88) * mm});
            skLineSegment(sketch, "E2.9.9.3", {"start": v(97.6, -24.63) * mm, "end": v(97.6, -43.88) * mm});
            skLineSegment(sketch, "E2.9.10.0", {"start": v(78.34, -3) * mm, "end": v(97.6, -3) * mm});
            skLineSegment(sketch, "E2.9.10.1", {"start": v(78.34, -22.24) * mm, "end": v(97.6, -22.24) * mm});
            skLineSegment(sketch, "E2.9.10.2", {"start": v(78.34, -3) * mm, "end": v(78.34, -22.24) * mm});
            skLineSegment(sketch, "E2.9.10.3", {"start": v(97.6, -3) * mm, "end": v(97.6, -22.24) * mm});
            skLineSegment(sketch, "E2.9.11.0", {"start": v(78.34, 18.65) * mm, "end": v(97.6, 18.65) * mm});
            skLineSegment(sketch, "E2.9.11.1", {"start": v(78.34, -0.6) * mm, "end": v(97.6, -0.6) * mm});
            skLineSegment(sketch, "E2.9.11.2", {"start": v(78.34, 18.65) * mm, "end": v(78.34, -0.6) * mm});
            skLineSegment(sketch, "E2.9.11.3", {"start": v(97.6, 18.65) * mm, "end": v(97.6, -0.6) * mm});
            skLineSegment(sketch, "E2.9.12.0", {"start": v(78.34, 40.3) * mm, "end": v(97.6, 40.3) * mm});
            skLineSegment(sketch, "E2.9.12.1", {"start": v(78.34, 21.04) * mm, "end": v(97.6, 21.04) * mm});
            skLineSegment(sketch, "E2.9.12.2", {"start": v(78.34, 40.3) * mm, "end": v(78.34, 21.04) * mm});
            skLineSegment(sketch, "E2.9.12.3", {"start": v(97.6, 40.3) * mm, "end": v(97.6, 21.04) * mm});
            skLineSegment(sketch, "E2.9.13.0", {"start": v(78.34, 61.93) * mm, "end": v(97.6, 61.93) * mm});
            skLineSegment(sketch, "E2.9.13.1", {"start": v(78.34, 42.68) * mm, "end": v(97.6, 42.68) * mm});
            skLineSegment(sketch, "E2.9.13.2", {"start": v(78.34, 61.93) * mm, "end": v(78.34, 42.68) * mm});
            skLineSegment(sketch, "E2.9.13.3", {"start": v(97.6, 61.93) * mm, "end": v(97.6, 42.68) * mm});
            skLineSegment(sketch, "E2.9.14.0", {"start": v(78.34, 83.57) * mm, "end": v(97.6, 83.57) * mm});
            skLineSegment(sketch, "E2.9.14.1", {"start": v(78.34, 64.32) * mm, "end": v(97.6, 64.32) * mm});
            skLineSegment(sketch, "E2.9.14.2", {"start": v(78.34, 83.57) * mm, "end": v(78.34, 64.32) * mm});
            skLineSegment(sketch, "E2.9.14.3", {"start": v(97.6, 83.57) * mm, "end": v(97.6, 64.32) * mm});
            skLineSegment(sketch, "E2.9.15.0", {"start": v(78.34, 105.21) * mm, "end": v(97.6, 105.21) * mm});
            skLineSegment(sketch, "E2.9.15.1", {"start": v(78.34, 85.96) * mm, "end": v(97.6, 85.96) * mm});
            skLineSegment(sketch, "E2.9.15.2", {"start": v(78.34, 105.21) * mm, "end": v(78.34, 85.96) * mm});
            skLineSegment(sketch, "E2.9.15.3", {"start": v(97.6, 105.21) * mm, "end": v(97.6, 85.96) * mm});
            skLineSegment(sketch, "E2.9.16.0", {"start": v(78.34, 126.85) * mm, "end": v(97.6, 126.85) * mm});
            skLineSegment(sketch, "E2.9.16.1", {"start": v(78.34, 107.6) * mm, "end": v(97.6, 107.6) * mm});
            skLineSegment(sketch, "E2.9.16.2", {"start": v(78.34, 126.85) * mm, "end": v(78.34, 107.6) * mm});
            skLineSegment(sketch, "E2.9.16.3", {"start": v(97.6, 126.85) * mm, "end": v(97.6, 107.6) * mm});
            skLineSegment(sketch, "E2.9.17.0", {"start": v(78.34, 148.5) * mm, "end": v(97.6, 148.5) * mm});
            skLineSegment(sketch, "E2.9.17.1", {"start": v(78.34, 129.24) * mm, "end": v(97.6, 129.24) * mm});
            skLineSegment(sketch, "E2.9.17.2", {"start": v(78.34, 148.5) * mm, "end": v(78.34, 129.24) * mm});
            skLineSegment(sketch, "E2.9.17.3", {"start": v(97.6, 148.5) * mm, "end": v(97.6, 129.24) * mm});
            skLineSegment(sketch, "E2.9.18.0", {"start": v(78.34, 170.14) * mm, "end": v(97.6, 170.14) * mm});
            skLineSegment(sketch, "E2.9.18.1", {"start": v(78.34, 150.88) * mm, "end": v(97.6, 150.88) * mm});
            skLineSegment(sketch, "E2.9.18.2", {"start": v(78.34, 170.14) * mm, "end": v(78.34, 150.88) * mm});
            skLineSegment(sketch, "E2.9.18.3", {"start": v(97.6, 170.14) * mm, "end": v(97.6, 150.88) * mm});
            skLineSegment(sketch, "E2.9.19.0", {"start": v(78.34, 191.78) * mm, "end": v(97.6, 191.78) * mm});
            skLineSegment(sketch, "E2.9.19.1", {"start": v(78.34, 172.52) * mm, "end": v(97.6, 172.52) * mm});
            skLineSegment(sketch, "E2.9.19.2", {"start": v(78.34, 191.78) * mm, "end": v(78.34, 172.52) * mm});
            skLineSegment(sketch, "E2.9.19.3", {"start": v(97.6, 191.78) * mm, "end": v(97.6, 172.52) * mm});
            skLineSegment(sketch, "E2.9.20.0", {"start": v(78.34, 213.42) * mm, "end": v(97.6, 213.42) * mm});
            skLineSegment(sketch, "E2.9.20.1", {"start": v(78.34, 194.16) * mm, "end": v(97.6, 194.16) * mm});
            skLineSegment(sketch, "E2.9.20.2", {"start": v(78.34, 213.42) * mm, "end": v(78.34, 194.16) * mm});
            skLineSegment(sketch, "E2.9.20.3", {"start": v(97.6, 213.42) * mm, "end": v(97.6, 194.16) * mm});
            skLineSegment(sketch, "E2.9.21.0", {"start": v(78.34, 235.06) * mm, "end": v(97.6, 235.06) * mm});
            skLineSegment(sketch, "E2.9.21.1", {"start": v(78.34, 215.8) * mm, "end": v(97.6, 215.8) * mm});
            skLineSegment(sketch, "E2.9.21.2", {"start": v(78.34, 235.06) * mm, "end": v(78.34, 215.8) * mm});
            skLineSegment(sketch, "E2.9.21.3", {"start": v(97.6, 235.06) * mm, "end": v(97.6, 215.8) * mm});
            skLineSegment(sketch, "E2.9.22.0", {"start": v(78.34, 256.7) * mm, "end": v(97.6, 256.7) * mm});
            skLineSegment(sketch, "E2.9.22.1", {"start": v(78.34, 237.45) * mm, "end": v(97.6, 237.45) * mm});
            skLineSegment(sketch, "E2.9.22.2", {"start": v(78.34, 256.7) * mm, "end": v(78.34, 237.45) * mm});
            skLineSegment(sketch, "E2.9.22.3", {"start": v(97.6, 256.7) * mm, "end": v(97.6, 237.45) * mm});
            skLineSegment(sketch, "E2.9.23.0", {"start": v(78.34, 278.34) * mm, "end": v(97.6, 278.34) * mm});
            skLineSegment(sketch, "E2.9.23.1", {"start": v(78.34, 259.09) * mm, "end": v(97.6, 259.09) * mm});
            skLineSegment(sketch, "E2.9.23.2", {"start": v(78.34, 278.34) * mm, "end": v(78.34, 259.09) * mm});
            skLineSegment(sketch, "E2.9.23.3", {"start": v(97.6, 278.34) * mm, "end": v(97.6, 259.09) * mm});
            skLineSegment(sketch, "E2.10.0.0", {"start": v(99.98, -219.4) * mm, "end": v(119.23, -219.4) * mm});
            skLineSegment(sketch, "E2.10.0.1", {"start": v(99.98, -238.65) * mm, "end": v(119.23, -238.65) * mm});
            skLineSegment(sketch, "E2.10.0.2", {"start": v(99.98, -219.4) * mm, "end": v(99.98, -238.65) * mm});
            skLineSegment(sketch, "E2.10.0.3", {"start": v(119.23, -219.4) * mm, "end": v(119.23, -238.65) * mm});
            skLineSegment(sketch, "E2.10.1.0", {"start": v(99.98, -197.76) * mm, "end": v(119.23, -197.76) * mm});
            skLineSegment(sketch, "E2.10.1.1", {"start": v(99.98, -217.01) * mm, "end": v(119.23, -217.01) * mm});
            skLineSegment(sketch, "E2.10.1.2", {"start": v(99.98, -197.76) * mm, "end": v(99.98, -217.01) * mm});
            skLineSegment(sketch, "E2.10.1.3", {"start": v(119.23, -197.76) * mm, "end": v(119.23, -217.01) * mm});
            skLineSegment(sketch, "E2.10.2.0", {"start": v(99.98, -176.12) * mm, "end": v(119.23, -176.12) * mm});
            skLineSegment(sketch, "E2.10.2.1", {"start": v(99.98, -195.37) * mm, "end": v(119.23, -195.37) * mm});
            skLineSegment(sketch, "E2.10.2.2", {"start": v(99.98, -176.12) * mm, "end": v(99.98, -195.37) * mm});
            skLineSegment(sketch, "E2.10.2.3", {"start": v(119.23, -176.12) * mm, "end": v(119.23, -195.37) * mm});
            skLineSegment(sketch, "E2.10.3.0", {"start": v(99.98, -154.48) * mm, "end": v(119.23, -154.48) * mm});
            skLineSegment(sketch, "E2.10.3.1", {"start": v(99.98, -173.73) * mm, "end": v(119.23, -173.73) * mm});
            skLineSegment(sketch, "E2.10.3.2", {"start": v(99.98, -154.48) * mm, "end": v(99.98, -173.73) * mm});
            skLineSegment(sketch, "E2.10.3.3", {"start": v(119.23, -154.48) * mm, "end": v(119.23, -173.73) * mm});
            skLineSegment(sketch, "E2.10.4.0", {"start": v(99.98, -132.84) * mm, "end": v(119.23, -132.84) * mm});
            skLineSegment(sketch, "E2.10.4.1", {"start": v(99.98, -152.09) * mm, "end": v(119.23, -152.09) * mm});
            skLineSegment(sketch, "E2.10.4.2", {"start": v(99.98, -132.84) * mm, "end": v(99.98, -152.09) * mm});
            skLineSegment(sketch, "E2.10.4.3", {"start": v(119.23, -132.84) * mm, "end": v(119.23, -152.09) * mm});
            skLineSegment(sketch, "E2.10.5.0", {"start": v(99.98, -111.2) * mm, "end": v(119.23, -111.2) * mm});
            skLineSegment(sketch, "E2.10.5.1", {"start": v(99.98, -130.45) * mm, "end": v(119.23, -130.45) * mm});
            skLineSegment(sketch, "E2.10.5.2", {"start": v(99.98, -111.2) * mm, "end": v(99.98, -130.45) * mm});
            skLineSegment(sketch, "E2.10.5.3", {"start": v(119.23, -111.2) * mm, "end": v(119.23, -130.45) * mm});
            skLineSegment(sketch, "E2.10.6.0", {"start": v(99.98, -89.55) * mm, "end": v(119.23, -89.55) * mm});
            skLineSegment(sketch, "E2.10.6.1", {"start": v(99.98, -108.8) * mm, "end": v(119.23, -108.8) * mm});
            skLineSegment(sketch, "E2.10.6.2", {"start": v(99.98, -89.55) * mm, "end": v(99.98, -108.8) * mm});
            skLineSegment(sketch, "E2.10.6.3", {"start": v(119.23, -89.55) * mm, "end": v(119.23, -108.8) * mm});
            skLineSegment(sketch, "E2.10.7.0", {"start": v(99.98, -67.91) * mm, "end": v(119.23, -67.91) * mm});
            skLineSegment(sketch, "E2.10.7.1", {"start": v(99.98, -87.17) * mm, "end": v(119.23, -87.17) * mm});
            skLineSegment(sketch, "E2.10.7.2", {"start": v(99.98, -67.91) * mm, "end": v(99.98, -87.17) * mm});
            skLineSegment(sketch, "E2.10.7.3", {"start": v(119.23, -67.91) * mm, "end": v(119.23, -87.17) * mm});
            skLineSegment(sketch, "E2.10.8.0", {"start": v(99.98, -46.27) * mm, "end": v(119.23, -46.27) * mm});
            skLineSegment(sketch, "E2.10.8.1", {"start": v(99.98, -65.53) * mm, "end": v(119.23, -65.53) * mm});
            skLineSegment(sketch, "E2.10.8.2", {"start": v(99.98, -46.27) * mm, "end": v(99.98, -65.53) * mm});
            skLineSegment(sketch, "E2.10.8.3", {"start": v(119.23, -46.27) * mm, "end": v(119.23, -65.53) * mm});
            skLineSegment(sketch, "E2.10.9.0", {"start": v(99.98, -24.63) * mm, "end": v(119.23, -24.63) * mm});
            skLineSegment(sketch, "E2.10.9.1", {"start": v(99.98, -43.88) * mm, "end": v(119.23, -43.88) * mm});
            skLineSegment(sketch, "E2.10.9.2", {"start": v(99.98, -24.63) * mm, "end": v(99.98, -43.88) * mm});
            skLineSegment(sketch, "E2.10.9.3", {"start": v(119.23, -24.63) * mm, "end": v(119.23, -43.88) * mm});
            skLineSegment(sketch, "E2.10.10.0", {"start": v(99.98, -3) * mm, "end": v(119.23, -3) * mm});
            skLineSegment(sketch, "E2.10.10.1", {"start": v(99.98, -22.24) * mm, "end": v(119.23, -22.24) * mm});
            skLineSegment(sketch, "E2.10.10.2", {"start": v(99.98, -3) * mm, "end": v(99.98, -22.24) * mm});
            skLineSegment(sketch, "E2.10.10.3", {"start": v(119.23, -3) * mm, "end": v(119.23, -22.24) * mm});
            skLineSegment(sketch, "E2.10.11.0", {"start": v(99.98, 18.65) * mm, "end": v(119.23, 18.65) * mm});
            skLineSegment(sketch, "E2.10.11.1", {"start": v(99.98, -0.6) * mm, "end": v(119.23, -0.6) * mm});
            skLineSegment(sketch, "E2.10.11.2", {"start": v(99.98, 18.65) * mm, "end": v(99.98, -0.6) * mm});
            skLineSegment(sketch, "E2.10.11.3", {"start": v(119.23, 18.65) * mm, "end": v(119.23, -0.6) * mm});
            skLineSegment(sketch, "E2.10.12.0", {"start": v(99.98, 40.3) * mm, "end": v(119.23, 40.3) * mm});
            skLineSegment(sketch, "E2.10.12.1", {"start": v(99.98, 21.04) * mm, "end": v(119.23, 21.04) * mm});
            skLineSegment(sketch, "E2.10.12.2", {"start": v(99.98, 40.3) * mm, "end": v(99.98, 21.04) * mm});
            skLineSegment(sketch, "E2.10.12.3", {"start": v(119.23, 40.3) * mm, "end": v(119.23, 21.04) * mm});
            skLineSegment(sketch, "E2.10.13.0", {"start": v(99.98, 61.93) * mm, "end": v(119.23, 61.93) * mm});
            skLineSegment(sketch, "E2.10.13.1", {"start": v(99.98, 42.68) * mm, "end": v(119.23, 42.68) * mm});
            skLineSegment(sketch, "E2.10.13.2", {"start": v(99.98, 61.93) * mm, "end": v(99.98, 42.68) * mm});
            skLineSegment(sketch, "E2.10.13.3", {"start": v(119.23, 61.93) * mm, "end": v(119.23, 42.68) * mm});
            skLineSegment(sketch, "E2.10.14.0", {"start": v(99.98, 83.57) * mm, "end": v(119.23, 83.57) * mm});
            skLineSegment(sketch, "E2.10.14.1", {"start": v(99.98, 64.32) * mm, "end": v(119.23, 64.32) * mm});
            skLineSegment(sketch, "E2.10.14.2", {"start": v(99.98, 83.57) * mm, "end": v(99.98, 64.32) * mm});
            skLineSegment(sketch, "E2.10.14.3", {"start": v(119.23, 83.57) * mm, "end": v(119.23, 64.32) * mm});
            skLineSegment(sketch, "E2.10.15.0", {"start": v(99.98, 105.21) * mm, "end": v(119.23, 105.21) * mm});
            skLineSegment(sketch, "E2.10.15.1", {"start": v(99.98, 85.96) * mm, "end": v(119.23, 85.96) * mm});
            skLineSegment(sketch, "E2.10.15.2", {"start": v(99.98, 105.21) * mm, "end": v(99.98, 85.96) * mm});
            skLineSegment(sketch, "E2.10.15.3", {"start": v(119.23, 105.21) * mm, "end": v(119.23, 85.96) * mm});
            skLineSegment(sketch, "E2.10.16.0", {"start": v(99.98, 126.85) * mm, "end": v(119.23, 126.85) * mm});
            skLineSegment(sketch, "E2.10.16.1", {"start": v(99.98, 107.6) * mm, "end": v(119.23, 107.6) * mm});
            skLineSegment(sketch, "E2.10.16.2", {"start": v(99.98, 126.85) * mm, "end": v(99.98, 107.6) * mm});
            skLineSegment(sketch, "E2.10.16.3", {"start": v(119.23, 126.85) * mm, "end": v(119.23, 107.6) * mm});
            skLineSegment(sketch, "E2.10.17.0", {"start": v(99.98, 148.5) * mm, "end": v(119.23, 148.5) * mm});
            skLineSegment(sketch, "E2.10.17.1", {"start": v(99.98, 129.24) * mm, "end": v(119.23, 129.24) * mm});
            skLineSegment(sketch, "E2.10.17.2", {"start": v(99.98, 148.5) * mm, "end": v(99.98, 129.24) * mm});
            skLineSegment(sketch, "E2.10.17.3", {"start": v(119.23, 148.5) * mm, "end": v(119.23, 129.24) * mm});
            skLineSegment(sketch, "E2.10.18.0", {"start": v(99.98, 170.14) * mm, "end": v(119.23, 170.14) * mm});
            skLineSegment(sketch, "E2.10.18.1", {"start": v(99.98, 150.88) * mm, "end": v(119.23, 150.88) * mm});
            skLineSegment(sketch, "E2.10.18.2", {"start": v(99.98, 170.14) * mm, "end": v(99.98, 150.88) * mm});
            skLineSegment(sketch, "E2.10.18.3", {"start": v(119.23, 170.14) * mm, "end": v(119.23, 150.88) * mm});
            skLineSegment(sketch, "E2.10.19.0", {"start": v(99.98, 191.78) * mm, "end": v(119.23, 191.78) * mm});
            skLineSegment(sketch, "E2.10.19.1", {"start": v(99.98, 172.52) * mm, "end": v(119.23, 172.52) * mm});
            skLineSegment(sketch, "E2.10.19.2", {"start": v(99.98, 191.78) * mm, "end": v(99.98, 172.52) * mm});
            skLineSegment(sketch, "E2.10.19.3", {"start": v(119.23, 191.78) * mm, "end": v(119.23, 172.52) * mm});
            skLineSegment(sketch, "E2.10.20.0", {"start": v(99.98, 213.42) * mm, "end": v(119.23, 213.42) * mm});
            skLineSegment(sketch, "E2.10.20.1", {"start": v(99.98, 194.16) * mm, "end": v(119.23, 194.16) * mm});
            skLineSegment(sketch, "E2.10.20.2", {"start": v(99.98, 213.42) * mm, "end": v(99.98, 194.16) * mm});
            skLineSegment(sketch, "E2.10.20.3", {"start": v(119.23, 213.42) * mm, "end": v(119.23, 194.16) * mm});
            skLineSegment(sketch, "E2.10.21.0", {"start": v(99.98, 235.06) * mm, "end": v(119.23, 235.06) * mm});
            skLineSegment(sketch, "E2.10.21.1", {"start": v(99.98, 215.8) * mm, "end": v(119.23, 215.8) * mm});
            skLineSegment(sketch, "E2.10.21.2", {"start": v(99.98, 235.06) * mm, "end": v(99.98, 215.8) * mm});
            skLineSegment(sketch, "E2.10.21.3", {"start": v(119.23, 235.06) * mm, "end": v(119.23, 215.8) * mm});
            skLineSegment(sketch, "E2.10.22.0", {"start": v(99.98, 256.7) * mm, "end": v(119.23, 256.7) * mm});
            skLineSegment(sketch, "E2.10.22.1", {"start": v(99.98, 237.45) * mm, "end": v(119.23, 237.45) * mm});
            skLineSegment(sketch, "E2.10.22.2", {"start": v(99.98, 256.7) * mm, "end": v(99.98, 237.45) * mm});
            skLineSegment(sketch, "E2.10.22.3", {"start": v(119.23, 256.7) * mm, "end": v(119.23, 237.45) * mm});
            skLineSegment(sketch, "E2.10.23.0", {"start": v(99.98, 278.34) * mm, "end": v(119.23, 278.34) * mm});
            skLineSegment(sketch, "E2.10.23.1", {"start": v(99.98, 259.09) * mm, "end": v(119.23, 259.09) * mm});
            skLineSegment(sketch, "E2.10.23.2", {"start": v(99.98, 278.34) * mm, "end": v(99.98, 259.09) * mm});
            skLineSegment(sketch, "E2.10.23.3", {"start": v(119.23, 278.34) * mm, "end": v(119.23, 259.09) * mm});
            skLineSegment(sketch, "E2.11.0.0", {"start": v(121.62, -219.4) * mm, "end": v(140.87, -219.4) * mm});
            skLineSegment(sketch, "E2.11.0.1", {"start": v(121.62, -238.65) * mm, "end": v(140.87, -238.65) * mm});
            skLineSegment(sketch, "E2.11.0.2", {"start": v(121.62, -219.4) * mm, "end": v(121.62, -238.65) * mm});
            skLineSegment(sketch, "E2.11.0.3", {"start": v(140.87, -219.4) * mm, "end": v(140.87, -238.65) * mm});
            skLineSegment(sketch, "E2.11.1.0", {"start": v(121.62, -197.76) * mm, "end": v(140.87, -197.76) * mm});
            skLineSegment(sketch, "E2.11.1.1", {"start": v(121.62, -217.01) * mm, "end": v(140.87, -217.01) * mm});
            skLineSegment(sketch, "E2.11.1.2", {"start": v(121.62, -197.76) * mm, "end": v(121.62, -217.01) * mm});
            skLineSegment(sketch, "E2.11.1.3", {"start": v(140.87, -197.76) * mm, "end": v(140.87, -217.01) * mm});
            skLineSegment(sketch, "E2.11.2.0", {"start": v(121.62, -176.12) * mm, "end": v(140.87, -176.12) * mm});
            skLineSegment(sketch, "E2.11.2.1", {"start": v(121.62, -195.37) * mm, "end": v(140.87, -195.37) * mm});
            skLineSegment(sketch, "E2.11.2.2", {"start": v(121.62, -176.12) * mm, "end": v(121.62, -195.37) * mm});
            skLineSegment(sketch, "E2.11.2.3", {"start": v(140.87, -176.12) * mm, "end": v(140.87, -195.37) * mm});
            skLineSegment(sketch, "E2.11.3.0", {"start": v(121.62, -154.48) * mm, "end": v(140.87, -154.48) * mm});
            skLineSegment(sketch, "E2.11.3.1", {"start": v(121.62, -173.73) * mm, "end": v(140.87, -173.73) * mm});
            skLineSegment(sketch, "E2.11.3.2", {"start": v(121.62, -154.48) * mm, "end": v(121.62, -173.73) * mm});
            skLineSegment(sketch, "E2.11.3.3", {"start": v(140.87, -154.48) * mm, "end": v(140.87, -173.73) * mm});
            skLineSegment(sketch, "E2.11.4.0", {"start": v(121.62, -132.84) * mm, "end": v(140.87, -132.84) * mm});
            skLineSegment(sketch, "E2.11.4.1", {"start": v(121.62, -152.09) * mm, "end": v(140.87, -152.09) * mm});
            skLineSegment(sketch, "E2.11.4.2", {"start": v(121.62, -132.84) * mm, "end": v(121.62, -152.09) * mm});
            skLineSegment(sketch, "E2.11.4.3", {"start": v(140.87, -132.84) * mm, "end": v(140.87, -152.09) * mm});
            skLineSegment(sketch, "E2.11.5.0", {"start": v(121.62, -111.2) * mm, "end": v(140.87, -111.2) * mm});
            skLineSegment(sketch, "E2.11.5.1", {"start": v(121.62, -130.45) * mm, "end": v(140.87, -130.45) * mm});
            skLineSegment(sketch, "E2.11.5.2", {"start": v(121.62, -111.2) * mm, "end": v(121.62, -130.45) * mm});
            skLineSegment(sketch, "E2.11.5.3", {"start": v(140.87, -111.2) * mm, "end": v(140.87, -130.45) * mm});
            skLineSegment(sketch, "E2.11.6.0", {"start": v(121.62, -89.55) * mm, "end": v(140.87, -89.55) * mm});
            skLineSegment(sketch, "E2.11.6.1", {"start": v(121.62, -108.8) * mm, "end": v(140.87, -108.8) * mm});
            skLineSegment(sketch, "E2.11.6.2", {"start": v(121.62, -89.55) * mm, "end": v(121.62, -108.8) * mm});
            skLineSegment(sketch, "E2.11.6.3", {"start": v(140.87, -89.55) * mm, "end": v(140.87, -108.8) * mm});
            skLineSegment(sketch, "E2.11.7.0", {"start": v(121.62, -67.91) * mm, "end": v(140.87, -67.91) * mm});
            skLineSegment(sketch, "E2.11.7.1", {"start": v(121.62, -87.17) * mm, "end": v(140.87, -87.17) * mm});
            skLineSegment(sketch, "E2.11.7.2", {"start": v(121.62, -67.91) * mm, "end": v(121.62, -87.17) * mm});
            skLineSegment(sketch, "E2.11.7.3", {"start": v(140.87, -67.91) * mm, "end": v(140.87, -87.17) * mm});
            skLineSegment(sketch, "E2.11.8.0", {"start": v(121.62, -46.27) * mm, "end": v(140.87, -46.27) * mm});
            skLineSegment(sketch, "E2.11.8.1", {"start": v(121.62, -65.53) * mm, "end": v(140.87, -65.53) * mm});
            skLineSegment(sketch, "E2.11.8.2", {"start": v(121.62, -46.27) * mm, "end": v(121.62, -65.53) * mm});
            skLineSegment(sketch, "E2.11.8.3", {"start": v(140.87, -46.27) * mm, "end": v(140.87, -65.53) * mm});
            skLineSegment(sketch, "E2.11.9.0", {"start": v(121.62, -24.63) * mm, "end": v(140.87, -24.63) * mm});
            skLineSegment(sketch, "E2.11.9.1", {"start": v(121.62, -43.88) * mm, "end": v(140.87, -43.88) * mm});
            skLineSegment(sketch, "E2.11.9.2", {"start": v(121.62, -24.63) * mm, "end": v(121.62, -43.88) * mm});
            skLineSegment(sketch, "E2.11.9.3", {"start": v(140.87, -24.63) * mm, "end": v(140.87, -43.88) * mm});
            skLineSegment(sketch, "E2.11.10.0", {"start": v(121.62, -3) * mm, "end": v(140.87, -3) * mm});
            skLineSegment(sketch, "E2.11.10.1", {"start": v(121.62, -22.24) * mm, "end": v(140.87, -22.24) * mm});
            skLineSegment(sketch, "E2.11.10.2", {"start": v(121.62, -3) * mm, "end": v(121.62, -22.24) * mm});
            skLineSegment(sketch, "E2.11.10.3", {"start": v(140.87, -3) * mm, "end": v(140.87, -22.24) * mm});
            skLineSegment(sketch, "E2.11.11.0", {"start": v(121.62, 18.65) * mm, "end": v(140.87, 18.65) * mm});
            skLineSegment(sketch, "E2.11.11.1", {"start": v(121.62, -0.6) * mm, "end": v(140.87, -0.6) * mm});
            skLineSegment(sketch, "E2.11.11.2", {"start": v(121.62, 18.65) * mm, "end": v(121.62, -0.6) * mm});
            skLineSegment(sketch, "E2.11.11.3", {"start": v(140.87, 18.65) * mm, "end": v(140.87, -0.6) * mm});
            skLineSegment(sketch, "E2.11.12.0", {"start": v(121.62, 40.3) * mm, "end": v(140.87, 40.3) * mm});
            skLineSegment(sketch, "E2.11.12.1", {"start": v(121.62, 21.04) * mm, "end": v(140.87, 21.04) * mm});
            skLineSegment(sketch, "E2.11.12.2", {"start": v(121.62, 40.3) * mm, "end": v(121.62, 21.04) * mm});
            skLineSegment(sketch, "E2.11.12.3", {"start": v(140.87, 40.3) * mm, "end": v(140.87, 21.04) * mm});
            skLineSegment(sketch, "E2.11.13.0", {"start": v(121.62, 61.93) * mm, "end": v(140.87, 61.93) * mm});
            skLineSegment(sketch, "E2.11.13.1", {"start": v(121.62, 42.68) * mm, "end": v(140.87, 42.68) * mm});
            skLineSegment(sketch, "E2.11.13.2", {"start": v(121.62, 61.93) * mm, "end": v(121.62, 42.68) * mm});
            skLineSegment(sketch, "E2.11.13.3", {"start": v(140.87, 61.93) * mm, "end": v(140.87, 42.68) * mm});
            skLineSegment(sketch, "E2.11.14.0", {"start": v(121.62, 83.57) * mm, "end": v(140.87, 83.57) * mm});
            skLineSegment(sketch, "E2.11.14.1", {"start": v(121.62, 64.32) * mm, "end": v(140.87, 64.32) * mm});
            skLineSegment(sketch, "E2.11.14.2", {"start": v(121.62, 83.57) * mm, "end": v(121.62, 64.32) * mm});
            skLineSegment(sketch, "E2.11.14.3", {"start": v(140.87, 83.57) * mm, "end": v(140.87, 64.32) * mm});
            skLineSegment(sketch, "E2.11.15.0", {"start": v(121.62, 105.21) * mm, "end": v(140.87, 105.21) * mm});
            skLineSegment(sketch, "E2.11.15.1", {"start": v(121.62, 85.96) * mm, "end": v(140.87, 85.96) * mm});
            skLineSegment(sketch, "E2.11.15.2", {"start": v(121.62, 105.21) * mm, "end": v(121.62, 85.96) * mm});
            skLineSegment(sketch, "E2.11.15.3", {"start": v(140.87, 105.21) * mm, "end": v(140.87, 85.96) * mm});
            skLineSegment(sketch, "E2.11.16.0", {"start": v(121.62, 126.85) * mm, "end": v(140.87, 126.85) * mm});
            skLineSegment(sketch, "E2.11.16.1", {"start": v(121.62, 107.6) * mm, "end": v(140.87, 107.6) * mm});
            skLineSegment(sketch, "E2.11.16.2", {"start": v(121.62, 126.85) * mm, "end": v(121.62, 107.6) * mm});
            skLineSegment(sketch, "E2.11.16.3", {"start": v(140.87, 126.85) * mm, "end": v(140.87, 107.6) * mm});
            skLineSegment(sketch, "E2.11.17.0", {"start": v(121.62, 148.5) * mm, "end": v(140.87, 148.5) * mm});
            skLineSegment(sketch, "E2.11.17.1", {"start": v(121.62, 129.24) * mm, "end": v(140.87, 129.24) * mm});
            skLineSegment(sketch, "E2.11.17.2", {"start": v(121.62, 148.5) * mm, "end": v(121.62, 129.24) * mm});
            skLineSegment(sketch, "E2.11.17.3", {"start": v(140.87, 148.5) * mm, "end": v(140.87, 129.24) * mm});
            skLineSegment(sketch, "E2.11.18.0", {"start": v(121.62, 170.14) * mm, "end": v(140.87, 170.14) * mm});
            skLineSegment(sketch, "E2.11.18.1", {"start": v(121.62, 150.88) * mm, "end": v(140.87, 150.88) * mm});
            skLineSegment(sketch, "E2.11.18.2", {"start": v(121.62, 170.14) * mm, "end": v(121.62, 150.88) * mm});
            skLineSegment(sketch, "E2.11.18.3", {"start": v(140.87, 170.14) * mm, "end": v(140.87, 150.88) * mm});
            skLineSegment(sketch, "E2.11.19.0", {"start": v(121.62, 191.78) * mm, "end": v(140.87, 191.78) * mm});
            skLineSegment(sketch, "E2.11.19.1", {"start": v(121.62, 172.52) * mm, "end": v(140.87, 172.52) * mm});
            skLineSegment(sketch, "E2.11.19.2", {"start": v(121.62, 191.78) * mm, "end": v(121.62, 172.52) * mm});
            skLineSegment(sketch, "E2.11.19.3", {"start": v(140.87, 191.78) * mm, "end": v(140.87, 172.52) * mm});
            skLineSegment(sketch, "E2.11.20.0", {"start": v(121.62, 213.42) * mm, "end": v(140.87, 213.42) * mm});
            skLineSegment(sketch, "E2.11.20.1", {"start": v(121.62, 194.16) * mm, "end": v(140.87, 194.16) * mm});
            skLineSegment(sketch, "E2.11.20.2", {"start": v(121.62, 213.42) * mm, "end": v(121.62, 194.16) * mm});
            skLineSegment(sketch, "E2.11.20.3", {"start": v(140.87, 213.42) * mm, "end": v(140.87, 194.16) * mm});
            skLineSegment(sketch, "E2.11.21.0", {"start": v(121.62, 235.06) * mm, "end": v(140.87, 235.06) * mm});
            skLineSegment(sketch, "E2.11.21.1", {"start": v(121.62, 215.8) * mm, "end": v(140.87, 215.8) * mm});
            skLineSegment(sketch, "E2.11.21.2", {"start": v(121.62, 235.06) * mm, "end": v(121.62, 215.8) * mm});
            skLineSegment(sketch, "E2.11.21.3", {"start": v(140.87, 235.06) * mm, "end": v(140.87, 215.8) * mm});
            skLineSegment(sketch, "E2.11.22.0", {"start": v(121.62, 256.7) * mm, "end": v(140.87, 256.7) * mm});
            skLineSegment(sketch, "E2.11.22.1", {"start": v(121.62, 237.45) * mm, "end": v(140.87, 237.45) * mm});
            skLineSegment(sketch, "E2.11.22.2", {"start": v(121.62, 256.7) * mm, "end": v(121.62, 237.45) * mm});
            skLineSegment(sketch, "E2.11.22.3", {"start": v(140.87, 256.7) * mm, "end": v(140.87, 237.45) * mm});
            skLineSegment(sketch, "E2.11.23.0", {"start": v(121.62, 278.34) * mm, "end": v(140.87, 278.34) * mm});
            skLineSegment(sketch, "E2.11.23.1", {"start": v(121.62, 259.09) * mm, "end": v(140.87, 259.09) * mm});
            skLineSegment(sketch, "E2.11.23.2", {"start": v(121.62, 278.34) * mm, "end": v(121.62, 259.09) * mm});
            skLineSegment(sketch, "E2.11.23.3", {"start": v(140.87, 278.34) * mm, "end": v(140.87, 259.09) * mm});
            skLineSegment(sketch, "E2.direction1", {"start": v(-116.43, -238.65) * mm, "end": v(-94.79, -238.65) * mm, "construction": true});
            skLineSegment(sketch, "E2.direction2", {"start": v(-116.43, -238.65) * mm, "end": v(-116.43, -217.01) * mm, "construction": true});
            skSolve(sketch);
        }
        {
            var Q0;
            Q0 = qSketchRegion(id + "F0", true);
            extrude(context, id + "F1", {"entities" : qUnion([Q0]), "depth" : 25.4 * mm, "offsetDistance" : 25.4 * mm});
        }
    });
